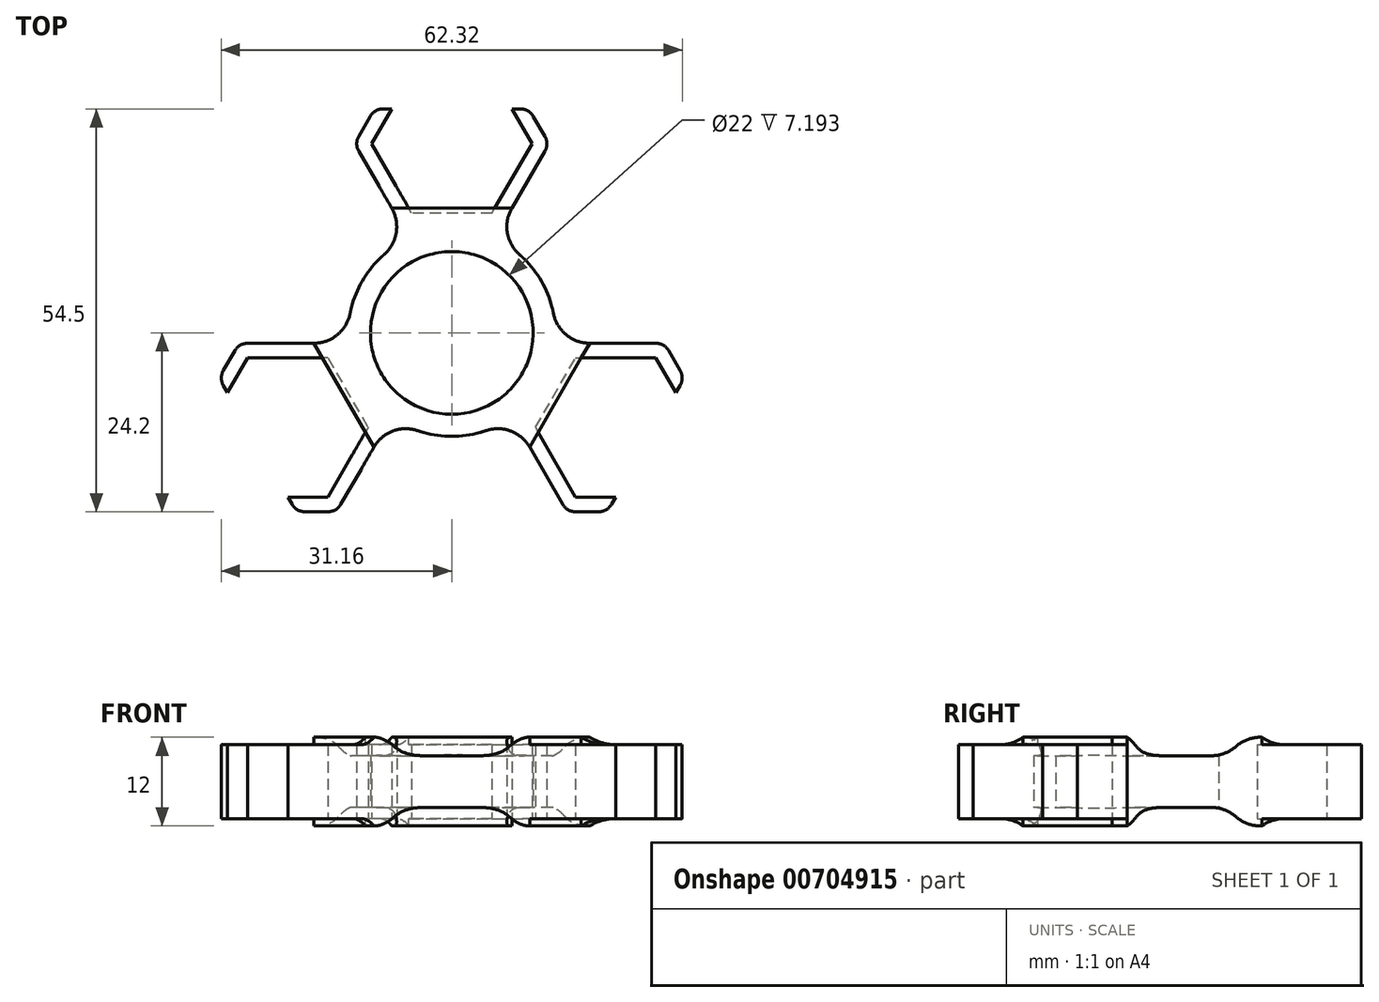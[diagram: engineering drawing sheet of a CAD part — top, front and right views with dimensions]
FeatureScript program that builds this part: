
annotation { "Feature Type Name" : "Feature", "Feature Type Description" : "" }
export const myFeature = defineFeature(function(context is Context, id is Id, definition is map)
    precondition{}
    {
        {
            var Q0;
            Q0=qCreatedBy(makeId("Top.planeOp"),FACE);
            var sketch = newSketch(context, id + "F0", { "sketchPlane" : qUnion([Q0])});
            skArc(sketch, "E0", {"start": v(9.53, 5.5) * mm, "mid": v(0, 11) * mm, "end": v(-9.53, 5.5) * mm});
            skCircle(sketch, "E1.cCircle", {"center": v(0, 25.6) * mm, "radius": 9.4 * mm, "construction": true});
            skLineSegment(sketch, "E1.0", {"start": v(-5.43, 35) * mm, "end": v(5.43, 35) * mm, "construction": true});
            skLineSegment(sketch, "E1.1", {"start": v(5.43, 35) * mm, "end": v(10.85, 25.6) * mm, "construction": true});
            skLineSegment(sketch, "E1.2", {"start": v(10.85, 25.6) * mm, "end": v(5.43, 16.2) * mm});
            skLineSegment(sketch, "E1.3", {"start": v(5.43, 16.2) * mm, "end": v(-5.43, 16.2) * mm});
            skLineSegment(sketch, "E1.4", {"start": v(-5.43, 16.2) * mm, "end": v(-10.85, 25.6) * mm});
            skLineSegment(sketch, "E1.5", {"start": v(-10.85, 25.6) * mm, "end": v(-5.43, 35) * mm, "construction": true});
            skPoint(sketch, "E1.0.midPoint", {"position": v(0, 35) * mm});
            skLineSegment(sketch, "E2", {"start": v(0, 0) * mm, "end": v(-9.53, 5.5) * mm, "construction": true});
            skLineSegment(sketch, "E3", {"start": v(9.53, 5.5) * mm, "end": v(0, 0) * mm, "construction": true});
            skLineSegment(sketch, "E4", {"start": v(-8.14, 30.3) * mm, "end": v(-9.3, 30.3) * mm});
            skArc(sketch, "E5", {"start": v(12.12, 7) * mm, "mid": v(9.4, 10.38) * mm, "end": v(5.75, 12.76) * mm});
            skLineSegment(sketch, "E6.0", {"start": v(-12.59, 26.6) * mm, "end": v(-11.03, 29.3) * mm});
            skLineSegment(sketch, "E6.1", {"start": v(-5.75, 12.76) * mm, "end": v(-12.59, 24.6) * mm});
            skPoint(sketch, "E7.visualSharp", {"position": v(-13.16, 25.6) * mm});
            skArc(sketch, "E7.filletArc", {"start": v(-12.59, 26.6) * mm, "mid": v(-12.85, 25.6) * mm, "end": v(-12.59, 24.6) * mm});
            skPoint(sketch, "E8.visualSharp", {"position": v(-10.45, 30.3) * mm});
            skArc(sketch, "E8.filletArc", {"start": v(-9.3, 30.3) * mm, "mid": v(-10.3, 30.03) * mm, "end": v(-11.03, 29.3) * mm});
            skLineSegment(sketch, "E9", {"start": v(0, 0) * mm, "end": v(0, 25.6) * mm, "construction": true});
            skLineSegment(sketch, "E10.MirrorCS", {"start": v(8.14, 30.3) * mm, "end": v(9.3, 30.3) * mm});
            skArc(sketch, "E11.MirrorCS", {"start": v(9.3, 30.3) * mm, "mid": v(10.3, 30.03) * mm, "end": v(11.03, 29.3) * mm});
            skLineSegment(sketch, "E12.MirrorCS", {"start": v(12.59, 26.6) * mm, "end": v(11.03, 29.3) * mm});
            skArc(sketch, "E13.MirrorCS", {"start": v(12.59, 26.6) * mm, "mid": v(12.85, 25.6) * mm, "end": v(12.59, 24.6) * mm});
            skLineSegment(sketch, "E14.MirrorCS", {"start": v(5.75, 12.76) * mm, "end": v(12.59, 24.6) * mm});
            skArc(sketch, "E15.trimOffspring", {"start": v(-5.75, 12.76) * mm, "mid": v(-9.4, 10.38) * mm, "end": v(-12.12, 7) * mm});
            skLineSegment(sketch, "E16", {"start": v(-8.14, 30.3) * mm, "end": v(-10.85, 25.6) * mm});
            skLineSegment(sketch, "E17", {"start": v(8.14, 30.3) * mm, "end": v(10.85, 25.6) * mm});
            skArc(sketch, "E18.1.0", {"start": v(-9.53, 5.5) * mm, "mid": v(-9.53, -5.5) * mm, "end": v(0, -11) * mm});
            skArc(sketch, "E18.1.1", {"start": v(-8.18, -11.36) * mm, "mid": v(-4.3, -13.32) * mm, "end": v(0, -14) * mm});
            skLineSegment(sketch, "E18.1.2", {"start": v(-8.18, -11.36) * mm, "end": v(-15.01, -23.2) * mm});
            skArc(sketch, "E18.1.3", {"start": v(-12.12, 7) * mm, "mid": v(-13.69, 2.94) * mm, "end": v(-13.93, -1.4) * mm});
            skLineSegment(sketch, "E18.1.4", {"start": v(-13.93, -1.4) * mm, "end": v(-27.6, -1.4) * mm});
            skLineSegment(sketch, "E18.1.5", {"start": v(-27.6, -3.4) * mm, "end": v(-16.74, -3.4) * mm});
            skLineSegment(sketch, "E18.1.6", {"start": v(-16.74, -3.4) * mm, "end": v(-11.32, -12.8) * mm});
            skLineSegment(sketch, "E18.1.7", {"start": v(-11.32, -12.8) * mm, "end": v(-16.74, -22.2) * mm});
            skArc(sketch, "E18.1.8", {"start": v(-16.74, -24.2) * mm, "mid": v(-15.74, -23.93) * mm, "end": v(-15.01, -23.2) * mm});
            skLineSegment(sketch, "E18.1.9", {"start": v(-16.74, -24.2) * mm, "end": v(-19.86, -24.2) * mm});
            skArc(sketch, "E18.1.10", {"start": v(-21.6, -23.2) * mm, "mid": v(-20.86, -23.93) * mm, "end": v(-19.86, -24.2) * mm});
            skLineSegment(sketch, "E18.1.11", {"start": v(-22.17, -22.2) * mm, "end": v(-21.6, -23.2) * mm});
            skLineSegment(sketch, "E18.1.12", {"start": v(-30.31, -8.1) * mm, "end": v(-30.89, -7.1) * mm});
            skArc(sketch, "E18.1.13", {"start": v(-30.89, -7.1) * mm, "mid": v(-31.16, -6.1) * mm, "end": v(-30.89, -5.1) * mm});
            skLineSegment(sketch, "E18.1.14", {"start": v(-29.33, -2.4) * mm, "end": v(-30.89, -5.1) * mm});
            skArc(sketch, "E18.1.15", {"start": v(-29.33, -2.4) * mm, "mid": v(-28.6, -1.67) * mm, "end": v(-27.6, -1.4) * mm});
            skArc(sketch, "E18.2.0", {"start": v(0, -11) * mm, "mid": v(9.53, -5.5) * mm, "end": v(9.53, 5.5) * mm});
            skArc(sketch, "E18.2.1", {"start": v(13.93, -1.4) * mm, "mid": v(13.69, 2.94) * mm, "end": v(12.12, 7) * mm});
            skLineSegment(sketch, "E18.2.2", {"start": v(13.93, -1.4) * mm, "end": v(27.6, -1.4) * mm});
            skArc(sketch, "E18.2.3", {"start": v(0, -14) * mm, "mid": v(4.3, -13.32) * mm, "end": v(8.18, -11.36) * mm});
            skLineSegment(sketch, "E18.2.4", {"start": v(8.18, -11.36) * mm, "end": v(15.01, -23.2) * mm});
            skLineSegment(sketch, "E18.2.5", {"start": v(16.74, -22.2) * mm, "end": v(11.32, -12.8) * mm});
            skLineSegment(sketch, "E18.2.6", {"start": v(11.32, -12.8) * mm, "end": v(16.74, -3.4) * mm});
            skLineSegment(sketch, "E18.2.7", {"start": v(16.74, -3.4) * mm, "end": v(27.6, -3.4) * mm});
            skArc(sketch, "E18.2.8", {"start": v(29.33, -2.4) * mm, "mid": v(28.6, -1.67) * mm, "end": v(27.6, -1.4) * mm});
            skLineSegment(sketch, "E18.2.9", {"start": v(29.33, -2.4) * mm, "end": v(30.89, -5.1) * mm});
            skArc(sketch, "E18.2.10", {"start": v(30.89, -7.1) * mm, "mid": v(31.16, -6.1) * mm, "end": v(30.89, -5.1) * mm});
            skLineSegment(sketch, "E18.2.11", {"start": v(30.31, -8.1) * mm, "end": v(30.89, -7.1) * mm});
            skLineSegment(sketch, "E18.2.12", {"start": v(22.17, -22.2) * mm, "end": v(21.6, -23.2) * mm});
            skArc(sketch, "E18.2.13", {"start": v(21.6, -23.2) * mm, "mid": v(20.86, -23.93) * mm, "end": v(19.86, -24.2) * mm});
            skLineSegment(sketch, "E18.2.14", {"start": v(16.74, -24.2) * mm, "end": v(19.86, -24.2) * mm});
            skArc(sketch, "E18.2.15", {"start": v(16.74, -24.2) * mm, "mid": v(15.74, -23.93) * mm, "end": v(15.01, -23.2) * mm});
            skLineSegment(sketch, "E19", {"start": v(27.6, -3.4) * mm, "end": v(30.31, -8.1) * mm});
            skLineSegment(sketch, "E20", {"start": v(16.74, -22.2) * mm, "end": v(22.17, -22.2) * mm});
            skLineSegment(sketch, "E21", {"start": v(-16.74, -22.2) * mm, "end": v(-22.17, -22.2) * mm});
            skLineSegment(sketch, "E22", {"start": v(-27.6, -3.4) * mm, "end": v(-30.31, -8.1) * mm});
            skSolve(sketch);
        }
        {
            var Q0;
            Q0 = qSketchRegion(id + "F0", true);
            extrude(context, id + "F1", {"entities" : qUnion([Q0]), "endBound" : BoundingType.SYMMETRIC, "depth" : 7 * mm, "offsetDistance" : 25 * mm});
        }
        {
            var Q0;
            Q0=makeQuery(id+"F1.opExtrude","SWEPT_EDGE",EDGE,{"disambiguationData":[OSD([sQuery(id+"F0.wireOp",EDGE,"E18.1.1"),sQuery(id+"F0.wireOp",EDGE,"E18.1.2")])]});
            var Q1;
            Q1=makeQuery(id+"F1.opExtrude","SWEPT_EDGE",EDGE,{"disambiguationData":[OSD([sQuery(id+"F0.wireOp",EDGE,"E18.2.3"),sQuery(id+"F0.wireOp",EDGE,"E18.2.4")])]});
            var Q2;
            Q2=makeQuery(id+"F1.opExtrude","SWEPT_EDGE",EDGE,{"disambiguationData":[OSD([sQuery(id+"F0.wireOp",EDGE,"E18.2.1"),sQuery(id+"F0.wireOp",EDGE,"E18.2.2")])]});
            var Q3;
            Q3=makeQuery(id+"F1.opExtrude","SWEPT_EDGE",EDGE,{"disambiguationData":[OSD([sQuery(id+"F0.wireOp",EDGE,"E5"),sQuery(id+"F0.wireOp",EDGE,"E14.MirrorCS")])]});
            var Q4;
            Q4=makeQuery(id+"F1.opExtrude","SWEPT_EDGE",EDGE,{"disambiguationData":[OSD([sQuery(id+"F0.wireOp",EDGE,"E6.1"),sQuery(id+"F0.wireOp",EDGE,"E15.trimOffspring")])]});
            var Q5;
            Q5=makeQuery(id+"F1.opExtrude","SWEPT_EDGE",EDGE,{"disambiguationData":[OSD([sQuery(id+"F0.wireOp",EDGE,"E18.1.3"),sQuery(id+"F0.wireOp",EDGE,"E18.1.4")])]});
            fillet(context, id + "F2", {"entities" : qUnion([Q0, Q1, Q2, Q3, Q4, Q5]), "radius" : 5 * mm, "tangentPropagation" : true, "allowEdgeOverflow" : false});
        }
        {
            var Q0;
            Q0=qCreatedBy(makeId("Top.planeOp"),FACE);
            var sketch = newSketch(context, id + "F3", { "sketchPlane" : qUnion([Q0])});
            skLineSegment(sketch, "E23.0", {"start": v(-12.59, 26.6) * mm, "end": v(-11.03, 29.3) * mm});
            skArc(sketch, "E23.1", {"start": v(-12.59, 26.6) * mm, "mid": v(-12.85, 25.6) * mm, "end": v(-12.59, 24.6) * mm});
            skLineSegment(sketch, "E23.2", {"start": v(-8.12, 16.86) * mm, "end": v(-12.59, 24.6) * mm});
            skLineSegment(sketch, "E23.3", {"start": v(-5.43, 16.2) * mm, "end": v(-10.85, 25.6) * mm});
            skLineSegment(sketch, "E23.4", {"start": v(-8.14, 30.3) * mm, "end": v(-10.85, 25.6) * mm});
            skArc(sketch, "E23.5", {"start": v(-9.3, 30.3) * mm, "mid": v(-10.3, 30.03) * mm, "end": v(-11.03, 29.3) * mm});
            skLineSegment(sketch, "E23.6", {"start": v(-8.14, 30.3) * mm, "end": v(-9.3, 30.3) * mm});
            skLineSegment(sketch, "E24", {"start": v(0, 15.22) * mm, "end": v(0, 32.5) * mm, "construction": true});
            skLineSegment(sketch, "E25.MirrorCS", {"start": v(5.43, 16.2) * mm, "end": v(10.85, 25.6) * mm});
            skLineSegment(sketch, "E26.MirrorCS", {"start": v(8.12, 16.86) * mm, "end": v(12.59, 24.6) * mm});
            skArc(sketch, "E27.MirrorCS", {"start": v(12.59, 26.6) * mm, "mid": v(12.85, 25.6) * mm, "end": v(12.59, 24.6) * mm});
            skLineSegment(sketch, "E28.MirrorCS", {"start": v(8.14, 30.3) * mm, "end": v(10.85, 25.6) * mm});
            skLineSegment(sketch, "E29.MirrorCS", {"start": v(12.59, 26.6) * mm, "end": v(11.03, 29.3) * mm});
            skArc(sketch, "E30.MirrorCS", {"start": v(9.3, 30.3) * mm, "mid": v(10.3, 30.03) * mm, "end": v(11.03, 29.3) * mm});
            skLineSegment(sketch, "E31.MirrorCS", {"start": v(8.14, 30.3) * mm, "end": v(9.3, 30.3) * mm});
            skLineSegment(sketch, "E32", {"start": v(5.43, 16.2) * mm, "end": v(-5.43, 16.2) * mm});
            skArc(sketch, "E33.0", {"start": v(8.12, 16.86) * mm, "mid": v(7.62, 15.65) * mm, "end": v(7.45, 14.36) * mm});
            skArc(sketch, "E33.1", {"start": v(-7.45, 14.36) * mm, "mid": v(-7.62, 15.65) * mm, "end": v(-8.12, 16.86) * mm});
            skLineSegment(sketch, "E34", {"start": v(7.45, 14.36) * mm, "end": v(-7.45, 14.36) * mm});
            skPoint(sketch, "E35.orphan", {"position": v(9.17, 10.58) * mm});
            skPoint(sketch, "E36.orphan", {"position": v(-9.17, 10.58) * mm});
            skLineSegment(sketch, "E37.1.0", {"start": v(13.18, -7.6) * mm, "end": v(28.15, -16.25) * mm, "construction": true});
            skLineSegment(sketch, "E37.1.1", {"start": v(18.66, -1.4) * mm, "end": v(27.6, -1.4) * mm});
            skLineSegment(sketch, "E37.1.2", {"start": v(11.32, -12.8) * mm, "end": v(16.74, -3.4) * mm});
            skLineSegment(sketch, "E37.1.3", {"start": v(8.71, -13.63) * mm, "end": v(16.16, -0.73) * mm});
            skLineSegment(sketch, "E37.1.4", {"start": v(10.54, -15.46) * mm, "end": v(15.01, -23.2) * mm});
            skLineSegment(sketch, "E37.1.5", {"start": v(11.32, -12.8) * mm, "end": v(16.74, -22.2) * mm});
            skLineSegment(sketch, "E37.1.6", {"start": v(16.74, -3.4) * mm, "end": v(27.6, -3.4) * mm});
            skLineSegment(sketch, "E37.1.7", {"start": v(30.31, -8.1) * mm, "end": v(27.6, -3.4) * mm});
            skLineSegment(sketch, "E37.1.8", {"start": v(22.17, -22.2) * mm, "end": v(16.74, -22.2) * mm});
            skLineSegment(sketch, "E37.1.9", {"start": v(29.33, -2.4) * mm, "end": v(30.89, -5.1) * mm});
            skLineSegment(sketch, "E37.1.10", {"start": v(30.31, -8.1) * mm, "end": v(30.89, -7.1) * mm});
            skArc(sketch, "E37.1.11", {"start": v(16.16, -0.73) * mm, "mid": v(17.36, -1.23) * mm, "end": v(18.66, -1.4) * mm});
            skArc(sketch, "E37.1.12", {"start": v(29.33, -2.4) * mm, "mid": v(28.6, -1.67) * mm, "end": v(27.6, -1.4) * mm});
            skLineSegment(sketch, "E37.1.13", {"start": v(22.17, -22.2) * mm, "end": v(21.6, -23.2) * mm});
            skArc(sketch, "E37.1.14", {"start": v(21.6, -23.2) * mm, "mid": v(20.86, -23.93) * mm, "end": v(19.86, -24.2) * mm});
            skArc(sketch, "E37.1.15", {"start": v(30.89, -7.1) * mm, "mid": v(31.16, -6.1) * mm, "end": v(30.89, -5.1) * mm});
            skArc(sketch, "E37.1.16", {"start": v(10.54, -15.46) * mm, "mid": v(9.75, -14.42) * mm, "end": v(8.71, -13.63) * mm});
            skLineSegment(sketch, "E37.1.17", {"start": v(16.74, -24.2) * mm, "end": v(19.86, -24.2) * mm});
            skArc(sketch, "E37.1.18", {"start": v(16.74, -24.2) * mm, "mid": v(15.74, -23.93) * mm, "end": v(15.01, -23.2) * mm});
            skLineSegment(sketch, "E37.2.0", {"start": v(-13.18, -7.6) * mm, "end": v(-28.15, -16.25) * mm, "construction": true});
            skLineSegment(sketch, "E37.2.1", {"start": v(-10.54, -15.46) * mm, "end": v(-15.01, -23.2) * mm});
            skLineSegment(sketch, "E37.2.2", {"start": v(-16.74, -3.4) * mm, "end": v(-11.32, -12.8) * mm});
            skLineSegment(sketch, "E37.2.3", {"start": v(-16.16, -0.73) * mm, "end": v(-8.71, -13.63) * mm});
            skLineSegment(sketch, "E37.2.4", {"start": v(-18.66, -1.4) * mm, "end": v(-27.6, -1.4) * mm});
            skLineSegment(sketch, "E37.2.5", {"start": v(-16.74, -3.4) * mm, "end": v(-27.6, -3.4) * mm});
            skLineSegment(sketch, "E37.2.6", {"start": v(-11.32, -12.8) * mm, "end": v(-16.74, -22.2) * mm});
            skLineSegment(sketch, "E37.2.7", {"start": v(-22.17, -22.2) * mm, "end": v(-16.74, -22.2) * mm});
            skLineSegment(sketch, "E37.2.8", {"start": v(-30.31, -8.1) * mm, "end": v(-27.6, -3.4) * mm});
            skLineSegment(sketch, "E37.2.9", {"start": v(-16.74, -24.2) * mm, "end": v(-19.86, -24.2) * mm});
            skLineSegment(sketch, "E37.2.10", {"start": v(-22.17, -22.2) * mm, "end": v(-21.6, -23.2) * mm});
            skArc(sketch, "E37.2.11", {"start": v(-8.71, -13.63) * mm, "mid": v(-9.75, -14.42) * mm, "end": v(-10.54, -15.46) * mm});
            skArc(sketch, "E37.2.12", {"start": v(-16.74, -24.2) * mm, "mid": v(-15.74, -23.93) * mm, "end": v(-15.01, -23.2) * mm});
            skLineSegment(sketch, "E37.2.13", {"start": v(-30.31, -8.1) * mm, "end": v(-30.89, -7.1) * mm});
            skArc(sketch, "E37.2.14", {"start": v(-30.89, -7.1) * mm, "mid": v(-31.16, -6.1) * mm, "end": v(-30.89, -5.1) * mm});
            skArc(sketch, "E37.2.15", {"start": v(-21.6, -23.2) * mm, "mid": v(-20.86, -23.93) * mm, "end": v(-19.86, -24.2) * mm});
            skArc(sketch, "E37.2.16", {"start": v(-18.66, -1.4) * mm, "mid": v(-17.36, -1.23) * mm, "end": v(-16.16, -0.73) * mm});
            skLineSegment(sketch, "E37.2.17", {"start": v(-29.33, -2.4) * mm, "end": v(-30.89, -5.1) * mm});
            skArc(sketch, "E37.2.18", {"start": v(-29.33, -2.4) * mm, "mid": v(-28.6, -1.67) * mm, "end": v(-27.6, -1.4) * mm});
            skPoint(sketch, "E37.center", {"position": v(0, 0) * mm});
            skLineSegment(sketch, "E37.anchor1", {"start": v(0, 0) * mm, "end": v(0, 32.5) * mm, "construction": true});
            skLineSegment(sketch, "E37.anchor2", {"start": v(0, 0) * mm, "end": v(-28.15, -16.25) * mm, "construction": true});
            skSolve(sketch);
        }
        {
            var Q0;
            Q0 = qSketchRegion(id + "F3", true);
            extrude(context, id + "F4", {"entities" : qUnion([Q0]), "operationType" : NewBodyOperationType.ADD, "endBound" : BoundingType.SYMMETRIC, "depth" : 10 * mm, "offsetDistance" : 25 * mm});
        }
        {
            var Q0;
            Q0=makeQuery(id+"F4.opExtrude","CAP_FACE",FACE,{"disambiguationData":[OSD([sQuery(id+"F3.wireOp",EDGE,"E23.0"),sQuery(id+"F3.wireOp",EDGE,"E23.1"),sQuery(id+"F3.wireOp",EDGE,"E23.2"),sQuery(id+"F3.wireOp",EDGE,"E23.3"),sQuery(id+"F3.wireOp",EDGE,"E23.4"),sQuery(id+"F3.wireOp",EDGE,"E23.5"),sQuery(id+"F3.wireOp",EDGE,"E23.6"),sQuery(id+"F3.wireOp",EDGE,"E25.MirrorCS"),sQuery(id+"F3.wireOp",EDGE,"E26.MirrorCS"),sQuery(id+"F3.wireOp",EDGE,"E27.MirrorCS"),sQuery(id+"F3.wireOp",EDGE,"E28.MirrorCS"),sQuery(id+"F3.wireOp",EDGE,"E29.MirrorCS"),sQuery(id+"F3.wireOp",EDGE,"E30.MirrorCS"),sQuery(id+"F3.wireOp",EDGE,"E31.MirrorCS"),sQuery(id+"F3.wireOp",EDGE,"E32"),sQuery(id+"F3.wireOp",EDGE,"E33.0"),sQuery(id+"F3.wireOp",EDGE,"E33.1"),sQuery(id+"F3.wireOp",EDGE,"E34")])],"isStart":false});
            var sketch = newSketch(context, id + "F5", { "sketchPlane" : qUnion([Q0])});
            skLineSegment(sketch, "E38.2", {"start": v(7.45, 14.36) * mm, "end": v(-7.45, 14.36) * mm});
            skArc(sketch, "E38.3", {"start": v(8.12, 16.86) * mm, "mid": v(7.62, 15.65) * mm, "end": v(7.45, 14.36) * mm});
            skArc(sketch, "E38.4", {"start": v(-7.45, 14.36) * mm, "mid": v(-7.62, 15.65) * mm, "end": v(-8.12, 16.86) * mm});
            skLineSegment(sketch, "E39", {"start": v(-8.12, 16.86) * mm, "end": v(8.12, 16.86) * mm});
            skPoint(sketch, "E38.6.end.orphan", {"position": v(-12.59, 24.6) * mm});
            skPoint(sketch, "E40.orphan", {"position": v(-10.85, 25.6) * mm});
            skPoint(sketch, "E41.orphan", {"position": v(10.85, 25.6) * mm});
            skPoint(sketch, "E38.7.end.orphan", {"position": v(12.59, 24.6) * mm});
            skPoint(sketch, "E38.1.end.orphan", {"position": v(-5.43, 16.2) * mm});
            skPoint(sketch, "E38.5.start.orphan", {"position": v(5.43, 16.2) * mm});
            skPoint(sketch, "E42.1.0", {"position": v(-11.32, -12.8) * mm});
            skLineSegment(sketch, "E42.1.1", {"start": v(-10.54, -15.46) * mm, "end": v(-18.66, -1.4) * mm});
            skPoint(sketch, "E42.1.2", {"position": v(-16.74, -3.4) * mm});
            skArc(sketch, "E42.1.3", {"start": v(-8.71, -13.63) * mm, "mid": v(-9.75, -14.42) * mm, "end": v(-10.54, -15.46) * mm});
            skArc(sketch, "E42.1.4", {"start": v(-18.66, -1.4) * mm, "mid": v(-17.36, -1.23) * mm, "end": v(-16.16, -0.73) * mm});
            skLineSegment(sketch, "E42.1.5", {"start": v(-16.16, -0.73) * mm, "end": v(-8.71, -13.63) * mm});
            skPoint(sketch, "E42.2.0", {"position": v(16.74, -3.4) * mm});
            skLineSegment(sketch, "E42.2.1", {"start": v(18.66, -1.4) * mm, "end": v(10.54, -15.46) * mm});
            skPoint(sketch, "E42.2.2", {"position": v(11.32, -12.8) * mm});
            skArc(sketch, "E42.2.3", {"start": v(16.16, -0.73) * mm, "mid": v(17.36, -1.23) * mm, "end": v(18.66, -1.4) * mm});
            skArc(sketch, "E42.2.4", {"start": v(10.54, -15.46) * mm, "mid": v(9.75, -14.42) * mm, "end": v(8.71, -13.63) * mm});
            skLineSegment(sketch, "E42.2.5", {"start": v(8.71, -13.63) * mm, "end": v(16.16, -0.73) * mm});
            skPoint(sketch, "E42.center", {"position": v(0, 0) * mm});
            skSolve(sketch);
        }
        {
            var Q0;
            Q0 = qSketchRegion(id + "F5", true);
            extrude(context, id + "F6", {"entities" : qUnion([Q0]), "depth" : 1 * mm, "offsetDistance" : 25 * mm});
        }
        {
            var Q0;
            Q0=makeQuery(id+"F6.opExtrude","SWEPT_BODY",BODY,{"disambiguationData":[OSD([sQuery(id+"F5.wireOp",EDGE,"E38.2"),sQuery(id+"F5.wireOp",EDGE,"E38.3"),sQuery(id+"F5.wireOp",EDGE,"E38.4"),sQuery(id+"F5.wireOp",EDGE,"E39")])]});
            var Q1;
            Q1=makeQuery(id+"F6.opExtrude","SWEPT_BODY",BODY,{"disambiguationData":[OSD([sQuery(id+"F5.wireOp",EDGE,"E42.1.1"),sQuery(id+"F5.wireOp",EDGE,"E42.1.3"),sQuery(id+"F5.wireOp",EDGE,"E42.1.4"),sQuery(id+"F5.wireOp",EDGE,"E42.1.5")])]});
            var Q2;
            Q2=makeQuery(id+"F6.opExtrude","SWEPT_BODY",BODY,{"disambiguationData":[OSD([sQuery(id+"F5.wireOp",EDGE,"E42.2.1"),sQuery(id+"F5.wireOp",EDGE,"E42.2.3"),sQuery(id+"F5.wireOp",EDGE,"E42.2.4"),sQuery(id+"F5.wireOp",EDGE,"E42.2.5")])]});
            var Q3;
            Q3=qCreatedBy(makeId("Top.planeOp"),FACE);
            mirror(context, id + "F7", {"operationType" : NewBodyOperationType.ADD, "entities" : qUnion([Q0, Q1, Q2]), "mirrorPlane" : qUnion([Q3])});
        }
        {
            var Q0;
            Q0=makeQuery(id+"F4.boolean.opBoolean","INTERSECT",EDGE,{"derivedFrom":[makeQuery(id+"F1.opExtrude","CAP_FACE",FACE,{"disambiguationData":[OSD([sQuery(id+"F0.wireOp",EDGE,"E0"),sQuery(id+"F0.wireOp",EDGE,"E1.2"),sQuery(id+"F0.wireOp",EDGE,"E1.3"),sQuery(id+"F0.wireOp",EDGE,"E1.4"),sQuery(id+"F0.wireOp",EDGE,"E4"),sQuery(id+"F0.wireOp",EDGE,"E5"),sQuery(id+"F0.wireOp",EDGE,"E6.0"),sQuery(id+"F0.wireOp",EDGE,"E6.1"),sQuery(id+"F0.wireOp",EDGE,"E7.filletArc"),sQuery(id+"F0.wireOp",EDGE,"E8.filletArc"),sQuery(id+"F0.wireOp",EDGE,"E10.MirrorCS"),sQuery(id+"F0.wireOp",EDGE,"E11.MirrorCS"),sQuery(id+"F0.wireOp",EDGE,"E12.MirrorCS"),sQuery(id+"F0.wireOp",EDGE,"E13.MirrorCS"),sQuery(id+"F0.wireOp",EDGE,"E14.MirrorCS"),sQuery(id+"F0.wireOp",EDGE,"E15.trimOffspring"),sQuery(id+"F0.wireOp",EDGE,"E16"),sQuery(id+"F0.wireOp",EDGE,"E17"),sQuery(id+"F0.wireOp",EDGE,"E18.1.0"),sQuery(id+"F0.wireOp",EDGE,"E18.1.1"),sQuery(id+"F0.wireOp",EDGE,"E18.1.2"),sQuery(id+"F0.wireOp",EDGE,"E18.1.3"),sQuery(id+"F0.wireOp",EDGE,"E18.1.4"),sQuery(id+"F0.wireOp",EDGE,"E18.1.5"),sQuery(id+"F0.wireOp",EDGE,"E18.1.6"),sQuery(id+"F0.wireOp",EDGE,"E18.1.7"),sQuery(id+"F0.wireOp",EDGE,"E18.1.8"),sQuery(id+"F0.wireOp",EDGE,"E18.1.9"),sQuery(id+"F0.wireOp",EDGE,"E18.1.10"),sQuery(id+"F0.wireOp",EDGE,"E18.1.11"),sQuery(id+"F0.wireOp",EDGE,"E18.1.12"),sQuery(id+"F0.wireOp",EDGE,"E18.1.13"),sQuery(id+"F0.wireOp",EDGE,"E18.1.14"),sQuery(id+"F0.wireOp",EDGE,"E18.1.15"),sQuery(id+"F0.wireOp",EDGE,"E18.2.0"),sQuery(id+"F0.wireOp",EDGE,"E18.2.1"),sQuery(id+"F0.wireOp",EDGE,"E18.2.2"),sQuery(id+"F0.wireOp",EDGE,"E18.2.3"),sQuery(id+"F0.wireOp",EDGE,"E18.2.4"),sQuery(id+"F0.wireOp",EDGE,"E18.2.5"),sQuery(id+"F0.wireOp",EDGE,"E18.2.6"),sQuery(id+"F0.wireOp",EDGE,"E18.2.7"),sQuery(id+"F0.wireOp",EDGE,"E18.2.8"),sQuery(id+"F0.wireOp",EDGE,"E18.2.9"),sQuery(id+"F0.wireOp",EDGE,"E18.2.10"),sQuery(id+"F0.wireOp",EDGE,"E18.2.11"),sQuery(id+"F0.wireOp",EDGE,"E18.2.12"),sQuery(id+"F0.wireOp",EDGE,"E18.2.13"),sQuery(id+"F0.wireOp",EDGE,"E18.2.14"),sQuery(id+"F0.wireOp",EDGE,"E18.2.15"),sQuery(id+"F0.wireOp",EDGE,"E19"),sQuery(id+"F0.wireOp",EDGE,"E20"),sQuery(id+"F0.wireOp",EDGE,"E21"),sQuery(id+"F0.wireOp",EDGE,"E22")])],"isStart":true}),makeQuery(id+"F4.opExtrude","SWEPT_FACE",FACE,{"disambiguationData":[OSD([sQuery(id+"F3.wireOp",EDGE,"E34")])]})]});
            var Q1;
            Q1=makeQuery(id+"F4.boolean.opBoolean","INTERSECT",EDGE,{"derivedFrom":[makeQuery(id+"F1.opExtrude","CAP_FACE",FACE,{"disambiguationData":[OSD([sQuery(id+"F0.wireOp",EDGE,"E0"),sQuery(id+"F0.wireOp",EDGE,"E1.2"),sQuery(id+"F0.wireOp",EDGE,"E1.3"),sQuery(id+"F0.wireOp",EDGE,"E1.4"),sQuery(id+"F0.wireOp",EDGE,"E4"),sQuery(id+"F0.wireOp",EDGE,"E5"),sQuery(id+"F0.wireOp",EDGE,"E6.0"),sQuery(id+"F0.wireOp",EDGE,"E6.1"),sQuery(id+"F0.wireOp",EDGE,"E7.filletArc"),sQuery(id+"F0.wireOp",EDGE,"E8.filletArc"),sQuery(id+"F0.wireOp",EDGE,"E10.MirrorCS"),sQuery(id+"F0.wireOp",EDGE,"E11.MirrorCS"),sQuery(id+"F0.wireOp",EDGE,"E12.MirrorCS"),sQuery(id+"F0.wireOp",EDGE,"E13.MirrorCS"),sQuery(id+"F0.wireOp",EDGE,"E14.MirrorCS"),sQuery(id+"F0.wireOp",EDGE,"E15.trimOffspring"),sQuery(id+"F0.wireOp",EDGE,"E16"),sQuery(id+"F0.wireOp",EDGE,"E17"),sQuery(id+"F0.wireOp",EDGE,"E18.1.0"),sQuery(id+"F0.wireOp",EDGE,"E18.1.1"),sQuery(id+"F0.wireOp",EDGE,"E18.1.2"),sQuery(id+"F0.wireOp",EDGE,"E18.1.3"),sQuery(id+"F0.wireOp",EDGE,"E18.1.4"),sQuery(id+"F0.wireOp",EDGE,"E18.1.5"),sQuery(id+"F0.wireOp",EDGE,"E18.1.6"),sQuery(id+"F0.wireOp",EDGE,"E18.1.7"),sQuery(id+"F0.wireOp",EDGE,"E18.1.8"),sQuery(id+"F0.wireOp",EDGE,"E18.1.9"),sQuery(id+"F0.wireOp",EDGE,"E18.1.10"),sQuery(id+"F0.wireOp",EDGE,"E18.1.11"),sQuery(id+"F0.wireOp",EDGE,"E18.1.12"),sQuery(id+"F0.wireOp",EDGE,"E18.1.13"),sQuery(id+"F0.wireOp",EDGE,"E18.1.14"),sQuery(id+"F0.wireOp",EDGE,"E18.1.15"),sQuery(id+"F0.wireOp",EDGE,"E18.2.0"),sQuery(id+"F0.wireOp",EDGE,"E18.2.1"),sQuery(id+"F0.wireOp",EDGE,"E18.2.2"),sQuery(id+"F0.wireOp",EDGE,"E18.2.3"),sQuery(id+"F0.wireOp",EDGE,"E18.2.4"),sQuery(id+"F0.wireOp",EDGE,"E18.2.5"),sQuery(id+"F0.wireOp",EDGE,"E18.2.6"),sQuery(id+"F0.wireOp",EDGE,"E18.2.7"),sQuery(id+"F0.wireOp",EDGE,"E18.2.8"),sQuery(id+"F0.wireOp",EDGE,"E18.2.9"),sQuery(id+"F0.wireOp",EDGE,"E18.2.10"),sQuery(id+"F0.wireOp",EDGE,"E18.2.11"),sQuery(id+"F0.wireOp",EDGE,"E18.2.12"),sQuery(id+"F0.wireOp",EDGE,"E18.2.13"),sQuery(id+"F0.wireOp",EDGE,"E18.2.14"),sQuery(id+"F0.wireOp",EDGE,"E18.2.15"),sQuery(id+"F0.wireOp",EDGE,"E19"),sQuery(id+"F0.wireOp",EDGE,"E20"),sQuery(id+"F0.wireOp",EDGE,"E21"),sQuery(id+"F0.wireOp",EDGE,"E22")])],"isStart":true}),makeQuery(id+"F4.opExtrude","SWEPT_FACE",FACE,{"disambiguationData":[OSD([sQuery(id+"F3.wireOp",EDGE,"E37.1.3")])]})]});
            var Q2;
            Q2=makeQuery(id+"F4.boolean.opBoolean","INTERSECT",EDGE,{"derivedFrom":[makeQuery(id+"F1.opExtrude","CAP_FACE",FACE,{"disambiguationData":[OSD([sQuery(id+"F0.wireOp",EDGE,"E0"),sQuery(id+"F0.wireOp",EDGE,"E1.2"),sQuery(id+"F0.wireOp",EDGE,"E1.3"),sQuery(id+"F0.wireOp",EDGE,"E1.4"),sQuery(id+"F0.wireOp",EDGE,"E4"),sQuery(id+"F0.wireOp",EDGE,"E5"),sQuery(id+"F0.wireOp",EDGE,"E6.0"),sQuery(id+"F0.wireOp",EDGE,"E6.1"),sQuery(id+"F0.wireOp",EDGE,"E7.filletArc"),sQuery(id+"F0.wireOp",EDGE,"E8.filletArc"),sQuery(id+"F0.wireOp",EDGE,"E10.MirrorCS"),sQuery(id+"F0.wireOp",EDGE,"E11.MirrorCS"),sQuery(id+"F0.wireOp",EDGE,"E12.MirrorCS"),sQuery(id+"F0.wireOp",EDGE,"E13.MirrorCS"),sQuery(id+"F0.wireOp",EDGE,"E14.MirrorCS"),sQuery(id+"F0.wireOp",EDGE,"E15.trimOffspring"),sQuery(id+"F0.wireOp",EDGE,"E16"),sQuery(id+"F0.wireOp",EDGE,"E17"),sQuery(id+"F0.wireOp",EDGE,"E18.1.0"),sQuery(id+"F0.wireOp",EDGE,"E18.1.1"),sQuery(id+"F0.wireOp",EDGE,"E18.1.2"),sQuery(id+"F0.wireOp",EDGE,"E18.1.3"),sQuery(id+"F0.wireOp",EDGE,"E18.1.4"),sQuery(id+"F0.wireOp",EDGE,"E18.1.5"),sQuery(id+"F0.wireOp",EDGE,"E18.1.6"),sQuery(id+"F0.wireOp",EDGE,"E18.1.7"),sQuery(id+"F0.wireOp",EDGE,"E18.1.8"),sQuery(id+"F0.wireOp",EDGE,"E18.1.9"),sQuery(id+"F0.wireOp",EDGE,"E18.1.10"),sQuery(id+"F0.wireOp",EDGE,"E18.1.11"),sQuery(id+"F0.wireOp",EDGE,"E18.1.12"),sQuery(id+"F0.wireOp",EDGE,"E18.1.13"),sQuery(id+"F0.wireOp",EDGE,"E18.1.14"),sQuery(id+"F0.wireOp",EDGE,"E18.1.15"),sQuery(id+"F0.wireOp",EDGE,"E18.2.0"),sQuery(id+"F0.wireOp",EDGE,"E18.2.1"),sQuery(id+"F0.wireOp",EDGE,"E18.2.2"),sQuery(id+"F0.wireOp",EDGE,"E18.2.3"),sQuery(id+"F0.wireOp",EDGE,"E18.2.4"),sQuery(id+"F0.wireOp",EDGE,"E18.2.5"),sQuery(id+"F0.wireOp",EDGE,"E18.2.6"),sQuery(id+"F0.wireOp",EDGE,"E18.2.7"),sQuery(id+"F0.wireOp",EDGE,"E18.2.8"),sQuery(id+"F0.wireOp",EDGE,"E18.2.9"),sQuery(id+"F0.wireOp",EDGE,"E18.2.10"),sQuery(id+"F0.wireOp",EDGE,"E18.2.11"),sQuery(id+"F0.wireOp",EDGE,"E18.2.12"),sQuery(id+"F0.wireOp",EDGE,"E18.2.13"),sQuery(id+"F0.wireOp",EDGE,"E18.2.14"),sQuery(id+"F0.wireOp",EDGE,"E18.2.15"),sQuery(id+"F0.wireOp",EDGE,"E19"),sQuery(id+"F0.wireOp",EDGE,"E20"),sQuery(id+"F0.wireOp",EDGE,"E21"),sQuery(id+"F0.wireOp",EDGE,"E22")])],"isStart":true}),makeQuery(id+"F4.opExtrude","SWEPT_FACE",FACE,{"disambiguationData":[OSD([sQuery(id+"F3.wireOp",EDGE,"E37.2.3")])]})]});
            var Q3;
            Q3=makeQuery(id+"F4.boolean.opBoolean","INTERSECT",EDGE,{"derivedFrom":[makeQuery(id+"F1.opExtrude","CAP_FACE",FACE,{"disambiguationData":[OSD([sQuery(id+"F0.wireOp",EDGE,"E0"),sQuery(id+"F0.wireOp",EDGE,"E1.2"),sQuery(id+"F0.wireOp",EDGE,"E1.3"),sQuery(id+"F0.wireOp",EDGE,"E1.4"),sQuery(id+"F0.wireOp",EDGE,"E4"),sQuery(id+"F0.wireOp",EDGE,"E5"),sQuery(id+"F0.wireOp",EDGE,"E6.0"),sQuery(id+"F0.wireOp",EDGE,"E6.1"),sQuery(id+"F0.wireOp",EDGE,"E7.filletArc"),sQuery(id+"F0.wireOp",EDGE,"E8.filletArc"),sQuery(id+"F0.wireOp",EDGE,"E10.MirrorCS"),sQuery(id+"F0.wireOp",EDGE,"E11.MirrorCS"),sQuery(id+"F0.wireOp",EDGE,"E12.MirrorCS"),sQuery(id+"F0.wireOp",EDGE,"E13.MirrorCS"),sQuery(id+"F0.wireOp",EDGE,"E14.MirrorCS"),sQuery(id+"F0.wireOp",EDGE,"E15.trimOffspring"),sQuery(id+"F0.wireOp",EDGE,"E16"),sQuery(id+"F0.wireOp",EDGE,"E17"),sQuery(id+"F0.wireOp",EDGE,"E18.1.0"),sQuery(id+"F0.wireOp",EDGE,"E18.1.1"),sQuery(id+"F0.wireOp",EDGE,"E18.1.2"),sQuery(id+"F0.wireOp",EDGE,"E18.1.3"),sQuery(id+"F0.wireOp",EDGE,"E18.1.4"),sQuery(id+"F0.wireOp",EDGE,"E18.1.5"),sQuery(id+"F0.wireOp",EDGE,"E18.1.6"),sQuery(id+"F0.wireOp",EDGE,"E18.1.7"),sQuery(id+"F0.wireOp",EDGE,"E18.1.8"),sQuery(id+"F0.wireOp",EDGE,"E18.1.9"),sQuery(id+"F0.wireOp",EDGE,"E18.1.10"),sQuery(id+"F0.wireOp",EDGE,"E18.1.11"),sQuery(id+"F0.wireOp",EDGE,"E18.1.12"),sQuery(id+"F0.wireOp",EDGE,"E18.1.13"),sQuery(id+"F0.wireOp",EDGE,"E18.1.14"),sQuery(id+"F0.wireOp",EDGE,"E18.1.15"),sQuery(id+"F0.wireOp",EDGE,"E18.2.0"),sQuery(id+"F0.wireOp",EDGE,"E18.2.1"),sQuery(id+"F0.wireOp",EDGE,"E18.2.2"),sQuery(id+"F0.wireOp",EDGE,"E18.2.3"),sQuery(id+"F0.wireOp",EDGE,"E18.2.4"),sQuery(id+"F0.wireOp",EDGE,"E18.2.5"),sQuery(id+"F0.wireOp",EDGE,"E18.2.6"),sQuery(id+"F0.wireOp",EDGE,"E18.2.7"),sQuery(id+"F0.wireOp",EDGE,"E18.2.8"),sQuery(id+"F0.wireOp",EDGE,"E18.2.9"),sQuery(id+"F0.wireOp",EDGE,"E18.2.10"),sQuery(id+"F0.wireOp",EDGE,"E18.2.11"),sQuery(id+"F0.wireOp",EDGE,"E18.2.12"),sQuery(id+"F0.wireOp",EDGE,"E18.2.13"),sQuery(id+"F0.wireOp",EDGE,"E18.2.14"),sQuery(id+"F0.wireOp",EDGE,"E18.2.15"),sQuery(id+"F0.wireOp",EDGE,"E19"),sQuery(id+"F0.wireOp",EDGE,"E20"),sQuery(id+"F0.wireOp",EDGE,"E21"),sQuery(id+"F0.wireOp",EDGE,"E22")])],"isStart":false}),makeQuery(id+"F4.opExtrude","SWEPT_FACE",FACE,{"disambiguationData":[OSD([sQuery(id+"F3.wireOp",EDGE,"E37.1.3")])]})]});
            var Q4;
            Q4=makeQuery(id+"F4.boolean.opBoolean","INTERSECT",EDGE,{"derivedFrom":[makeQuery(id+"F1.opExtrude","CAP_FACE",FACE,{"disambiguationData":[OSD([sQuery(id+"F0.wireOp",EDGE,"E0"),sQuery(id+"F0.wireOp",EDGE,"E1.2"),sQuery(id+"F0.wireOp",EDGE,"E1.3"),sQuery(id+"F0.wireOp",EDGE,"E1.4"),sQuery(id+"F0.wireOp",EDGE,"E4"),sQuery(id+"F0.wireOp",EDGE,"E5"),sQuery(id+"F0.wireOp",EDGE,"E6.0"),sQuery(id+"F0.wireOp",EDGE,"E6.1"),sQuery(id+"F0.wireOp",EDGE,"E7.filletArc"),sQuery(id+"F0.wireOp",EDGE,"E8.filletArc"),sQuery(id+"F0.wireOp",EDGE,"E10.MirrorCS"),sQuery(id+"F0.wireOp",EDGE,"E11.MirrorCS"),sQuery(id+"F0.wireOp",EDGE,"E12.MirrorCS"),sQuery(id+"F0.wireOp",EDGE,"E13.MirrorCS"),sQuery(id+"F0.wireOp",EDGE,"E14.MirrorCS"),sQuery(id+"F0.wireOp",EDGE,"E15.trimOffspring"),sQuery(id+"F0.wireOp",EDGE,"E16"),sQuery(id+"F0.wireOp",EDGE,"E17"),sQuery(id+"F0.wireOp",EDGE,"E18.1.0"),sQuery(id+"F0.wireOp",EDGE,"E18.1.1"),sQuery(id+"F0.wireOp",EDGE,"E18.1.2"),sQuery(id+"F0.wireOp",EDGE,"E18.1.3"),sQuery(id+"F0.wireOp",EDGE,"E18.1.4"),sQuery(id+"F0.wireOp",EDGE,"E18.1.5"),sQuery(id+"F0.wireOp",EDGE,"E18.1.6"),sQuery(id+"F0.wireOp",EDGE,"E18.1.7"),sQuery(id+"F0.wireOp",EDGE,"E18.1.8"),sQuery(id+"F0.wireOp",EDGE,"E18.1.9"),sQuery(id+"F0.wireOp",EDGE,"E18.1.10"),sQuery(id+"F0.wireOp",EDGE,"E18.1.11"),sQuery(id+"F0.wireOp",EDGE,"E18.1.12"),sQuery(id+"F0.wireOp",EDGE,"E18.1.13"),sQuery(id+"F0.wireOp",EDGE,"E18.1.14"),sQuery(id+"F0.wireOp",EDGE,"E18.1.15"),sQuery(id+"F0.wireOp",EDGE,"E18.2.0"),sQuery(id+"F0.wireOp",EDGE,"E18.2.1"),sQuery(id+"F0.wireOp",EDGE,"E18.2.2"),sQuery(id+"F0.wireOp",EDGE,"E18.2.3"),sQuery(id+"F0.wireOp",EDGE,"E18.2.4"),sQuery(id+"F0.wireOp",EDGE,"E18.2.5"),sQuery(id+"F0.wireOp",EDGE,"E18.2.6"),sQuery(id+"F0.wireOp",EDGE,"E18.2.7"),sQuery(id+"F0.wireOp",EDGE,"E18.2.8"),sQuery(id+"F0.wireOp",EDGE,"E18.2.9"),sQuery(id+"F0.wireOp",EDGE,"E18.2.10"),sQuery(id+"F0.wireOp",EDGE,"E18.2.11"),sQuery(id+"F0.wireOp",EDGE,"E18.2.12"),sQuery(id+"F0.wireOp",EDGE,"E18.2.13"),sQuery(id+"F0.wireOp",EDGE,"E18.2.14"),sQuery(id+"F0.wireOp",EDGE,"E18.2.15"),sQuery(id+"F0.wireOp",EDGE,"E19"),sQuery(id+"F0.wireOp",EDGE,"E20"),sQuery(id+"F0.wireOp",EDGE,"E21"),sQuery(id+"F0.wireOp",EDGE,"E22")])],"isStart":false}),makeQuery(id+"F4.opExtrude","SWEPT_FACE",FACE,{"disambiguationData":[OSD([sQuery(id+"F3.wireOp",EDGE,"E34")])]})]});
            var Q5;
            Q5=makeQuery(id+"F4.boolean.opBoolean","INTERSECT",EDGE,{"derivedFrom":[makeQuery(id+"F1.opExtrude","CAP_FACE",FACE,{"disambiguationData":[OSD([sQuery(id+"F0.wireOp",EDGE,"E0"),sQuery(id+"F0.wireOp",EDGE,"E1.2"),sQuery(id+"F0.wireOp",EDGE,"E1.3"),sQuery(id+"F0.wireOp",EDGE,"E1.4"),sQuery(id+"F0.wireOp",EDGE,"E4"),sQuery(id+"F0.wireOp",EDGE,"E5"),sQuery(id+"F0.wireOp",EDGE,"E6.0"),sQuery(id+"F0.wireOp",EDGE,"E6.1"),sQuery(id+"F0.wireOp",EDGE,"E7.filletArc"),sQuery(id+"F0.wireOp",EDGE,"E8.filletArc"),sQuery(id+"F0.wireOp",EDGE,"E10.MirrorCS"),sQuery(id+"F0.wireOp",EDGE,"E11.MirrorCS"),sQuery(id+"F0.wireOp",EDGE,"E12.MirrorCS"),sQuery(id+"F0.wireOp",EDGE,"E13.MirrorCS"),sQuery(id+"F0.wireOp",EDGE,"E14.MirrorCS"),sQuery(id+"F0.wireOp",EDGE,"E15.trimOffspring"),sQuery(id+"F0.wireOp",EDGE,"E16"),sQuery(id+"F0.wireOp",EDGE,"E17"),sQuery(id+"F0.wireOp",EDGE,"E18.1.0"),sQuery(id+"F0.wireOp",EDGE,"E18.1.1"),sQuery(id+"F0.wireOp",EDGE,"E18.1.2"),sQuery(id+"F0.wireOp",EDGE,"E18.1.3"),sQuery(id+"F0.wireOp",EDGE,"E18.1.4"),sQuery(id+"F0.wireOp",EDGE,"E18.1.5"),sQuery(id+"F0.wireOp",EDGE,"E18.1.6"),sQuery(id+"F0.wireOp",EDGE,"E18.1.7"),sQuery(id+"F0.wireOp",EDGE,"E18.1.8"),sQuery(id+"F0.wireOp",EDGE,"E18.1.9"),sQuery(id+"F0.wireOp",EDGE,"E18.1.10"),sQuery(id+"F0.wireOp",EDGE,"E18.1.11"),sQuery(id+"F0.wireOp",EDGE,"E18.1.12"),sQuery(id+"F0.wireOp",EDGE,"E18.1.13"),sQuery(id+"F0.wireOp",EDGE,"E18.1.14"),sQuery(id+"F0.wireOp",EDGE,"E18.1.15"),sQuery(id+"F0.wireOp",EDGE,"E18.2.0"),sQuery(id+"F0.wireOp",EDGE,"E18.2.1"),sQuery(id+"F0.wireOp",EDGE,"E18.2.2"),sQuery(id+"F0.wireOp",EDGE,"E18.2.3"),sQuery(id+"F0.wireOp",EDGE,"E18.2.4"),sQuery(id+"F0.wireOp",EDGE,"E18.2.5"),sQuery(id+"F0.wireOp",EDGE,"E18.2.6"),sQuery(id+"F0.wireOp",EDGE,"E18.2.7"),sQuery(id+"F0.wireOp",EDGE,"E18.2.8"),sQuery(id+"F0.wireOp",EDGE,"E18.2.9"),sQuery(id+"F0.wireOp",EDGE,"E18.2.10"),sQuery(id+"F0.wireOp",EDGE,"E18.2.11"),sQuery(id+"F0.wireOp",EDGE,"E18.2.12"),sQuery(id+"F0.wireOp",EDGE,"E18.2.13"),sQuery(id+"F0.wireOp",EDGE,"E18.2.14"),sQuery(id+"F0.wireOp",EDGE,"E18.2.15"),sQuery(id+"F0.wireOp",EDGE,"E19"),sQuery(id+"F0.wireOp",EDGE,"E20"),sQuery(id+"F0.wireOp",EDGE,"E21"),sQuery(id+"F0.wireOp",EDGE,"E22")])],"isStart":false}),makeQuery(id+"F4.opExtrude","SWEPT_FACE",FACE,{"disambiguationData":[OSD([sQuery(id+"F3.wireOp",EDGE,"E37.2.3")])]})]});
            fillet(context, id + "F8", {"entities" : qUnion([Q0, Q1, Q2, Q3, Q4, Q5]), "radius" : 5 * mm, "tangentPropagation" : true, "allowEdgeOverflow" : false});
        }
        {
            var Q0;
            {var subQ2=sQuery(id+"F5.wireOp",EDGE,"E42.2.1");var subQ3=sQuery(id+"F3.wireOp",EDGE,"E37.1.5");var subQ4=makeQuery(id+"F6.opExtrude","SWEPT_FACE",FACE,{"disambiguationData":[OSD([subQ2])]});var subQ5=sQuery(id+"F3.wireOp",EDGE,"E37.1.4");var subQ6=sQuery(id+"F0.wireOp",EDGE,"E18.2.4");var subQ7=sQuery(id+"F3.wireOp",EDGE,"E37.1.16");var subQ8=makeQuery(id+"F4.opExtrude","CAP_FACE",FACE,{"disambiguationData":[OSD([sQuery(id+"F3.wireOp",EDGE,"E37.1.1"),sQuery(id+"F3.wireOp",EDGE,"E37.1.2"),sQuery(id+"F3.wireOp",EDGE,"E37.1.3"),subQ5,subQ3,sQuery(id+"F3.wireOp",EDGE,"E37.1.6"),sQuery(id+"F3.wireOp",EDGE,"E37.1.7"),sQuery(id+"F3.wireOp",EDGE,"E37.1.8"),sQuery(id+"F3.wireOp",EDGE,"E37.1.9"),sQuery(id+"F3.wireOp",EDGE,"E37.1.10"),sQuery(id+"F3.wireOp",EDGE,"E37.1.11"),sQuery(id+"F3.wireOp",EDGE,"E37.1.12"),sQuery(id+"F3.wireOp",EDGE,"E37.1.13"),sQuery(id+"F3.wireOp",EDGE,"E37.1.14"),sQuery(id+"F3.wireOp",EDGE,"E37.1.15"),subQ7,sQuery(id+"F3.wireOp",EDGE,"E37.1.17"),sQuery(id+"F3.wireOp",EDGE,"E37.1.18")])],"isStart":false});Q0=makeQuery(id+"F7.boolean.opBoolean","SPLIT",EDGE,{"disambiguationData":[topologyDisambiguationEdgeConnected([subQ8,subQ4]),TD([makeQuery(id+"F1.opExtrude","SWEPT_FACE",FACE,{"disambiguationData":[OSD([subQ6])]})])],"derivedFrom":makeQuery(id+"F6.opExtrude","CAP_EDGE",EDGE,{"disambiguationData":[OSD([subQ2])],"isStart":true})});}
            var Q1;
            {var subQ0=sQuery(id+"F5.wireOp",EDGE,"E42.2.1");var subQ1=makeQuery(id+"F6.opExtrude","SWEPT_FACE",FACE,{"disambiguationData":[OSD([subQ0])]});var subQ2=sQuery(id+"F3.wireOp",EDGE,"E37.1.11");var subQ3=sQuery(id+"F3.wireOp",EDGE,"E37.1.6");var subQ5=sQuery(id+"F0.wireOp",EDGE,"E18.2.2");var subQ7=sQuery(id+"F3.wireOp",EDGE,"E37.1.1");var subQ8=makeQuery(id+"F4.opExtrude","CAP_FACE",FACE,{"disambiguationData":[OSD([subQ7,sQuery(id+"F3.wireOp",EDGE,"E37.1.2"),sQuery(id+"F3.wireOp",EDGE,"E37.1.3"),sQuery(id+"F3.wireOp",EDGE,"E37.1.4"),sQuery(id+"F3.wireOp",EDGE,"E37.1.5"),subQ3,sQuery(id+"F3.wireOp",EDGE,"E37.1.7"),sQuery(id+"F3.wireOp",EDGE,"E37.1.8"),sQuery(id+"F3.wireOp",EDGE,"E37.1.9"),sQuery(id+"F3.wireOp",EDGE,"E37.1.10"),subQ2,sQuery(id+"F3.wireOp",EDGE,"E37.1.12"),sQuery(id+"F3.wireOp",EDGE,"E37.1.13"),sQuery(id+"F3.wireOp",EDGE,"E37.1.14"),sQuery(id+"F3.wireOp",EDGE,"E37.1.15"),sQuery(id+"F3.wireOp",EDGE,"E37.1.16"),sQuery(id+"F3.wireOp",EDGE,"E37.1.17"),sQuery(id+"F3.wireOp",EDGE,"E37.1.18")])],"isStart":false});Q1=makeQuery(id+"F7.boolean.opBoolean","SPLIT",EDGE,{"disambiguationData":[topologyDisambiguationEdgeConnected([subQ8,subQ1]),TD([makeQuery(id+"F1.opExtrude","SWEPT_FACE",FACE,{"disambiguationData":[OSD([subQ5])]})])],"derivedFrom":makeQuery(id+"F6.opExtrude","CAP_EDGE",EDGE,{"disambiguationData":[OSD([subQ0])],"isStart":true})});}
            var Q2;
            {var subQ1=sQuery(id+"F5.wireOp",EDGE,"E42.2.1");var subQ2=sQuery(id+"F3.wireOp",EDGE,"E37.1.4");var subQ3=sQuery(id+"F0.wireOp",EDGE,"E18.2.4");var subQ4=makeQuery(id+"F7.opPattern","COPY",FACE,{"derivedFrom":makeQuery(id+"F6.opExtrude","SWEPT_FACE",FACE,{"disambiguationData":[OSD([subQ1])]}),"instanceName":"1"});var subQ6=sQuery(id+"F3.wireOp",EDGE,"E37.1.16");var subQ7=sQuery(id+"F3.wireOp",EDGE,"E37.1.5");var subQ8=makeQuery(id+"F4.opExtrude","CAP_FACE",FACE,{"disambiguationData":[OSD([sQuery(id+"F3.wireOp",EDGE,"E37.1.1"),sQuery(id+"F3.wireOp",EDGE,"E37.1.2"),sQuery(id+"F3.wireOp",EDGE,"E37.1.3"),subQ2,subQ7,sQuery(id+"F3.wireOp",EDGE,"E37.1.6"),sQuery(id+"F3.wireOp",EDGE,"E37.1.7"),sQuery(id+"F3.wireOp",EDGE,"E37.1.8"),sQuery(id+"F3.wireOp",EDGE,"E37.1.9"),sQuery(id+"F3.wireOp",EDGE,"E37.1.10"),sQuery(id+"F3.wireOp",EDGE,"E37.1.11"),sQuery(id+"F3.wireOp",EDGE,"E37.1.12"),sQuery(id+"F3.wireOp",EDGE,"E37.1.13"),sQuery(id+"F3.wireOp",EDGE,"E37.1.14"),sQuery(id+"F3.wireOp",EDGE,"E37.1.15"),subQ6,sQuery(id+"F3.wireOp",EDGE,"E37.1.17"),sQuery(id+"F3.wireOp",EDGE,"E37.1.18")])],"isStart":true});Q2=makeQuery(id+"F7.boolean.opBoolean","SPLIT",EDGE,{"disambiguationData":[topologyDisambiguationEdgeConnected([subQ8,subQ4]),TD([makeQuery(id+"F1.opExtrude","SWEPT_FACE",FACE,{"disambiguationData":[OSD([subQ3])]})])],"derivedFrom":makeQuery(id+"F7.opPattern","COPY",EDGE,{"derivedFrom":makeQuery(id+"F6.opExtrude","CAP_EDGE",EDGE,{"disambiguationData":[OSD([subQ1])],"isStart":true}),"instanceName":"1"})});}
            var Q3;
            {var subQ0=sQuery(id+"F3.wireOp",EDGE,"E37.1.6");var subQ1=sQuery(id+"F5.wireOp",EDGE,"E42.2.1");var subQ2=makeQuery(id+"F7.opPattern","COPY",FACE,{"derivedFrom":makeQuery(id+"F6.opExtrude","SWEPT_FACE",FACE,{"disambiguationData":[OSD([subQ1])]}),"instanceName":"1"});var subQ3=sQuery(id+"F3.wireOp",EDGE,"E37.1.11");var subQ4=sQuery(id+"F3.wireOp",EDGE,"E37.1.1");var subQ5=makeQuery(id+"F4.opExtrude","CAP_FACE",FACE,{"disambiguationData":[OSD([subQ4,sQuery(id+"F3.wireOp",EDGE,"E37.1.2"),sQuery(id+"F3.wireOp",EDGE,"E37.1.3"),sQuery(id+"F3.wireOp",EDGE,"E37.1.4"),sQuery(id+"F3.wireOp",EDGE,"E37.1.5"),subQ0,sQuery(id+"F3.wireOp",EDGE,"E37.1.7"),sQuery(id+"F3.wireOp",EDGE,"E37.1.8"),sQuery(id+"F3.wireOp",EDGE,"E37.1.9"),sQuery(id+"F3.wireOp",EDGE,"E37.1.10"),subQ3,sQuery(id+"F3.wireOp",EDGE,"E37.1.12"),sQuery(id+"F3.wireOp",EDGE,"E37.1.13"),sQuery(id+"F3.wireOp",EDGE,"E37.1.14"),sQuery(id+"F3.wireOp",EDGE,"E37.1.15"),sQuery(id+"F3.wireOp",EDGE,"E37.1.16"),sQuery(id+"F3.wireOp",EDGE,"E37.1.17"),sQuery(id+"F3.wireOp",EDGE,"E37.1.18")])],"isStart":true});var subQ6=sQuery(id+"F0.wireOp",EDGE,"E18.2.2");Q3=makeQuery(id+"F7.boolean.opBoolean","SPLIT",EDGE,{"disambiguationData":[topologyDisambiguationEdgeConnected([subQ5,subQ2]),TD([makeQuery(id+"F1.opExtrude","SWEPT_FACE",FACE,{"disambiguationData":[OSD([subQ6])]})])],"derivedFrom":makeQuery(id+"F7.opPattern","COPY",EDGE,{"derivedFrom":makeQuery(id+"F6.opExtrude","CAP_EDGE",EDGE,{"disambiguationData":[OSD([subQ1])],"isStart":true}),"instanceName":"1"})});}
            var Q4;
            {var subQ2=sQuery(id+"F5.wireOp",EDGE,"E39");var subQ3=sQuery(id+"F3.wireOp",EDGE,"E33.0");var subQ4=sQuery(id+"F3.wireOp",EDGE,"E25.MirrorCS");var subQ6=makeQuery(id+"F6.opExtrude","SWEPT_FACE",FACE,{"disambiguationData":[OSD([subQ2])]});var subQ7=sQuery(id+"F3.wireOp",EDGE,"E26.MirrorCS");var subQ8=makeQuery(id+"F4.opExtrude","CAP_FACE",FACE,{"disambiguationData":[OSD([sQuery(id+"F3.wireOp",EDGE,"E23.0"),sQuery(id+"F3.wireOp",EDGE,"E23.1"),sQuery(id+"F3.wireOp",EDGE,"E23.2"),sQuery(id+"F3.wireOp",EDGE,"E23.3"),sQuery(id+"F3.wireOp",EDGE,"E23.4"),sQuery(id+"F3.wireOp",EDGE,"E23.5"),sQuery(id+"F3.wireOp",EDGE,"E23.6"),subQ4,subQ7,sQuery(id+"F3.wireOp",EDGE,"E27.MirrorCS"),sQuery(id+"F3.wireOp",EDGE,"E28.MirrorCS"),sQuery(id+"F3.wireOp",EDGE,"E29.MirrorCS"),sQuery(id+"F3.wireOp",EDGE,"E30.MirrorCS"),sQuery(id+"F3.wireOp",EDGE,"E31.MirrorCS"),sQuery(id+"F3.wireOp",EDGE,"E32"),subQ3,sQuery(id+"F3.wireOp",EDGE,"E33.1"),sQuery(id+"F3.wireOp",EDGE,"E34")])],"isStart":false});Q4=makeQuery(id+"F7.boolean.opBoolean","SPLIT",EDGE,{"disambiguationData":[topologyDisambiguationEdgeConnected([subQ8,subQ6]),TD([makeQuery(id+"F1.opExtrude","SWEPT_FACE",FACE,{"disambiguationData":[OSD([sQuery(id+"F0.wireOp",EDGE,"E1.2")])]})])],"derivedFrom":makeQuery(id+"F6.opExtrude","CAP_EDGE",EDGE,{"disambiguationData":[OSD([subQ2])],"isStart":true})});}
            var Q5;
            {var subQ0=sQuery(id+"F5.wireOp",EDGE,"E39");var subQ1=makeQuery(id+"F6.opExtrude","SWEPT_FACE",FACE,{"disambiguationData":[OSD([subQ0])]});var subQ2=sQuery(id+"F3.wireOp",EDGE,"E33.1");var subQ5=sQuery(id+"F3.wireOp",EDGE,"E23.3");var subQ6=sQuery(id+"F3.wireOp",EDGE,"E23.2");var subQ8=makeQuery(id+"F4.opExtrude","CAP_FACE",FACE,{"disambiguationData":[OSD([sQuery(id+"F3.wireOp",EDGE,"E23.0"),sQuery(id+"F3.wireOp",EDGE,"E23.1"),subQ6,subQ5,sQuery(id+"F3.wireOp",EDGE,"E23.4"),sQuery(id+"F3.wireOp",EDGE,"E23.5"),sQuery(id+"F3.wireOp",EDGE,"E23.6"),sQuery(id+"F3.wireOp",EDGE,"E25.MirrorCS"),sQuery(id+"F3.wireOp",EDGE,"E26.MirrorCS"),sQuery(id+"F3.wireOp",EDGE,"E27.MirrorCS"),sQuery(id+"F3.wireOp",EDGE,"E28.MirrorCS"),sQuery(id+"F3.wireOp",EDGE,"E29.MirrorCS"),sQuery(id+"F3.wireOp",EDGE,"E30.MirrorCS"),sQuery(id+"F3.wireOp",EDGE,"E31.MirrorCS"),sQuery(id+"F3.wireOp",EDGE,"E32"),sQuery(id+"F3.wireOp",EDGE,"E33.0"),subQ2,sQuery(id+"F3.wireOp",EDGE,"E34")])],"isStart":false});Q5=makeQuery(id+"F7.boolean.opBoolean","SPLIT",EDGE,{"disambiguationData":[topologyDisambiguationEdgeConnected([subQ8,subQ1]),TD([makeQuery(id+"F1.opExtrude","SWEPT_FACE",FACE,{"disambiguationData":[OSD([sQuery(id+"F0.wireOp",EDGE,"E1.4")])]})])],"derivedFrom":makeQuery(id+"F6.opExtrude","CAP_EDGE",EDGE,{"disambiguationData":[OSD([subQ0])],"isStart":true})});}
            var Q6;
            {var subQ2=sQuery(id+"F3.wireOp",EDGE,"E33.0");var subQ3=sQuery(id+"F3.wireOp",EDGE,"E25.MirrorCS");var subQ5=sQuery(id+"F5.wireOp",EDGE,"E39");var subQ6=sQuery(id+"F3.wireOp",EDGE,"E26.MirrorCS");var subQ7=makeQuery(id+"F4.opExtrude","CAP_FACE",FACE,{"disambiguationData":[OSD([sQuery(id+"F3.wireOp",EDGE,"E23.0"),sQuery(id+"F3.wireOp",EDGE,"E23.1"),sQuery(id+"F3.wireOp",EDGE,"E23.2"),sQuery(id+"F3.wireOp",EDGE,"E23.3"),sQuery(id+"F3.wireOp",EDGE,"E23.4"),sQuery(id+"F3.wireOp",EDGE,"E23.5"),sQuery(id+"F3.wireOp",EDGE,"E23.6"),subQ3,subQ6,sQuery(id+"F3.wireOp",EDGE,"E27.MirrorCS"),sQuery(id+"F3.wireOp",EDGE,"E28.MirrorCS"),sQuery(id+"F3.wireOp",EDGE,"E29.MirrorCS"),sQuery(id+"F3.wireOp",EDGE,"E30.MirrorCS"),sQuery(id+"F3.wireOp",EDGE,"E31.MirrorCS"),sQuery(id+"F3.wireOp",EDGE,"E32"),subQ2,sQuery(id+"F3.wireOp",EDGE,"E33.1"),sQuery(id+"F3.wireOp",EDGE,"E34")])],"isStart":true});var subQ8=makeQuery(id+"F7.opPattern","COPY",FACE,{"derivedFrom":makeQuery(id+"F6.opExtrude","SWEPT_FACE",FACE,{"disambiguationData":[OSD([subQ5])]}),"instanceName":"1"});Q6=makeQuery(id+"F7.boolean.opBoolean","SPLIT",EDGE,{"disambiguationData":[topologyDisambiguationEdgeConnected([subQ7,subQ8]),TD([makeQuery(id+"F1.opExtrude","SWEPT_FACE",FACE,{"disambiguationData":[OSD([sQuery(id+"F0.wireOp",EDGE,"E1.2")])]})])],"derivedFrom":makeQuery(id+"F7.opPattern","COPY",EDGE,{"derivedFrom":makeQuery(id+"F6.opExtrude","CAP_EDGE",EDGE,{"disambiguationData":[OSD([subQ5])],"isStart":true}),"instanceName":"1"})});}
            var Q7;
            {var subQ2=sQuery(id+"F5.wireOp",EDGE,"E39");var subQ3=sQuery(id+"F3.wireOp",EDGE,"E33.1");var subQ4=sQuery(id+"F3.wireOp",EDGE,"E23.3");var subQ5=sQuery(id+"F3.wireOp",EDGE,"E23.2");var subQ6=makeQuery(id+"F4.opExtrude","CAP_FACE",FACE,{"disambiguationData":[OSD([sQuery(id+"F3.wireOp",EDGE,"E23.0"),sQuery(id+"F3.wireOp",EDGE,"E23.1"),subQ5,subQ4,sQuery(id+"F3.wireOp",EDGE,"E23.4"),sQuery(id+"F3.wireOp",EDGE,"E23.5"),sQuery(id+"F3.wireOp",EDGE,"E23.6"),sQuery(id+"F3.wireOp",EDGE,"E25.MirrorCS"),sQuery(id+"F3.wireOp",EDGE,"E26.MirrorCS"),sQuery(id+"F3.wireOp",EDGE,"E27.MirrorCS"),sQuery(id+"F3.wireOp",EDGE,"E28.MirrorCS"),sQuery(id+"F3.wireOp",EDGE,"E29.MirrorCS"),sQuery(id+"F3.wireOp",EDGE,"E30.MirrorCS"),sQuery(id+"F3.wireOp",EDGE,"E31.MirrorCS"),sQuery(id+"F3.wireOp",EDGE,"E32"),sQuery(id+"F3.wireOp",EDGE,"E33.0"),subQ3,sQuery(id+"F3.wireOp",EDGE,"E34")])],"isStart":true});var subQ7=makeQuery(id+"F7.opPattern","COPY",FACE,{"derivedFrom":makeQuery(id+"F6.opExtrude","SWEPT_FACE",FACE,{"disambiguationData":[OSD([subQ2])]}),"instanceName":"1"});Q7=makeQuery(id+"F7.boolean.opBoolean","SPLIT",EDGE,{"disambiguationData":[topologyDisambiguationEdgeConnected([subQ6,subQ7]),TD([makeQuery(id+"F1.opExtrude","SWEPT_FACE",FACE,{"disambiguationData":[OSD([sQuery(id+"F0.wireOp",EDGE,"E1.4")])]})])],"derivedFrom":makeQuery(id+"F7.opPattern","COPY",EDGE,{"derivedFrom":makeQuery(id+"F6.opExtrude","CAP_EDGE",EDGE,{"disambiguationData":[OSD([subQ2])],"isStart":true}),"instanceName":"1"})});}
            var Q8;
            {var subQ2=sQuery(id+"F3.wireOp",EDGE,"E37.2.5");var subQ3=sQuery(id+"F5.wireOp",EDGE,"E42.1.1");var subQ4=makeQuery(id+"F6.opExtrude","SWEPT_FACE",FACE,{"disambiguationData":[OSD([subQ3])]});var subQ5=sQuery(id+"F3.wireOp",EDGE,"E37.2.16");var subQ6=sQuery(id+"F3.wireOp",EDGE,"E37.2.4");var subQ7=makeQuery(id+"F4.opExtrude","CAP_FACE",FACE,{"disambiguationData":[OSD([sQuery(id+"F3.wireOp",EDGE,"E37.2.1"),sQuery(id+"F3.wireOp",EDGE,"E37.2.2"),sQuery(id+"F3.wireOp",EDGE,"E37.2.3"),subQ6,subQ2,sQuery(id+"F3.wireOp",EDGE,"E37.2.6"),sQuery(id+"F3.wireOp",EDGE,"E37.2.7"),sQuery(id+"F3.wireOp",EDGE,"E37.2.8"),sQuery(id+"F3.wireOp",EDGE,"E37.2.9"),sQuery(id+"F3.wireOp",EDGE,"E37.2.10"),sQuery(id+"F3.wireOp",EDGE,"E37.2.11"),sQuery(id+"F3.wireOp",EDGE,"E37.2.12"),sQuery(id+"F3.wireOp",EDGE,"E37.2.13"),sQuery(id+"F3.wireOp",EDGE,"E37.2.14"),sQuery(id+"F3.wireOp",EDGE,"E37.2.15"),subQ5,sQuery(id+"F3.wireOp",EDGE,"E37.2.17"),sQuery(id+"F3.wireOp",EDGE,"E37.2.18")])],"isStart":false});var subQ8=sQuery(id+"F0.wireOp",EDGE,"E18.1.4");Q8=makeQuery(id+"F7.boolean.opBoolean","SPLIT",EDGE,{"disambiguationData":[topologyDisambiguationEdgeConnected([subQ7,subQ4]),TD([makeQuery(id+"F1.opExtrude","SWEPT_FACE",FACE,{"disambiguationData":[OSD([subQ8])]})])],"derivedFrom":makeQuery(id+"F6.opExtrude","CAP_EDGE",EDGE,{"disambiguationData":[OSD([subQ3])],"isStart":true})});}
            var Q9;
            {var subQ0=sQuery(id+"F5.wireOp",EDGE,"E42.1.1");var subQ1=makeQuery(id+"F6.opExtrude","SWEPT_FACE",FACE,{"disambiguationData":[OSD([subQ0])]});var subQ2=sQuery(id+"F3.wireOp",EDGE,"E37.2.11");var subQ3=sQuery(id+"F3.wireOp",EDGE,"E37.2.6");var subQ4=sQuery(id+"F3.wireOp",EDGE,"E37.2.1");var subQ5=makeQuery(id+"F4.opExtrude","CAP_FACE",FACE,{"disambiguationData":[OSD([subQ4,sQuery(id+"F3.wireOp",EDGE,"E37.2.2"),sQuery(id+"F3.wireOp",EDGE,"E37.2.3"),sQuery(id+"F3.wireOp",EDGE,"E37.2.4"),sQuery(id+"F3.wireOp",EDGE,"E37.2.5"),subQ3,sQuery(id+"F3.wireOp",EDGE,"E37.2.7"),sQuery(id+"F3.wireOp",EDGE,"E37.2.8"),sQuery(id+"F3.wireOp",EDGE,"E37.2.9"),sQuery(id+"F3.wireOp",EDGE,"E37.2.10"),subQ2,sQuery(id+"F3.wireOp",EDGE,"E37.2.12"),sQuery(id+"F3.wireOp",EDGE,"E37.2.13"),sQuery(id+"F3.wireOp",EDGE,"E37.2.14"),sQuery(id+"F3.wireOp",EDGE,"E37.2.15"),sQuery(id+"F3.wireOp",EDGE,"E37.2.16"),sQuery(id+"F3.wireOp",EDGE,"E37.2.17"),sQuery(id+"F3.wireOp",EDGE,"E37.2.18")])],"isStart":false});var subQ8=sQuery(id+"F0.wireOp",EDGE,"E18.1.2");Q9=makeQuery(id+"F7.boolean.opBoolean","SPLIT",EDGE,{"disambiguationData":[topologyDisambiguationEdgeConnected([subQ5,subQ1]),TD([makeQuery(id+"F1.opExtrude","SWEPT_FACE",FACE,{"disambiguationData":[OSD([subQ8])]})])],"derivedFrom":makeQuery(id+"F6.opExtrude","CAP_EDGE",EDGE,{"disambiguationData":[OSD([subQ0])],"isStart":true})});}
            var Q10;
            {var subQ1=sQuery(id+"F5.wireOp",EDGE,"E42.1.1");var subQ2=makeQuery(id+"F7.opPattern","COPY",FACE,{"derivedFrom":makeQuery(id+"F6.opExtrude","SWEPT_FACE",FACE,{"disambiguationData":[OSD([subQ1])]}),"instanceName":"1"});var subQ4=sQuery(id+"F3.wireOp",EDGE,"E37.2.5");var subQ5=sQuery(id+"F3.wireOp",EDGE,"E37.2.4");var subQ6=sQuery(id+"F0.wireOp",EDGE,"E18.1.4");var subQ7=sQuery(id+"F3.wireOp",EDGE,"E37.2.16");var subQ8=makeQuery(id+"F4.opExtrude","CAP_FACE",FACE,{"disambiguationData":[OSD([sQuery(id+"F3.wireOp",EDGE,"E37.2.1"),sQuery(id+"F3.wireOp",EDGE,"E37.2.2"),sQuery(id+"F3.wireOp",EDGE,"E37.2.3"),subQ5,subQ4,sQuery(id+"F3.wireOp",EDGE,"E37.2.6"),sQuery(id+"F3.wireOp",EDGE,"E37.2.7"),sQuery(id+"F3.wireOp",EDGE,"E37.2.8"),sQuery(id+"F3.wireOp",EDGE,"E37.2.9"),sQuery(id+"F3.wireOp",EDGE,"E37.2.10"),sQuery(id+"F3.wireOp",EDGE,"E37.2.11"),sQuery(id+"F3.wireOp",EDGE,"E37.2.12"),sQuery(id+"F3.wireOp",EDGE,"E37.2.13"),sQuery(id+"F3.wireOp",EDGE,"E37.2.14"),sQuery(id+"F3.wireOp",EDGE,"E37.2.15"),subQ7,sQuery(id+"F3.wireOp",EDGE,"E37.2.17"),sQuery(id+"F3.wireOp",EDGE,"E37.2.18")])],"isStart":true});Q10=makeQuery(id+"F7.boolean.opBoolean","SPLIT",EDGE,{"disambiguationData":[topologyDisambiguationEdgeConnected([subQ8,subQ2]),TD([makeQuery(id+"F1.opExtrude","SWEPT_FACE",FACE,{"disambiguationData":[OSD([subQ6])]})])],"derivedFrom":makeQuery(id+"F7.opPattern","COPY",EDGE,{"derivedFrom":makeQuery(id+"F6.opExtrude","CAP_EDGE",EDGE,{"disambiguationData":[OSD([subQ1])],"isStart":true}),"instanceName":"1"})});}
            var Q11;
            {var subQ0=sQuery(id+"F5.wireOp",EDGE,"E42.1.1");var subQ1=makeQuery(id+"F7.opPattern","COPY",FACE,{"derivedFrom":makeQuery(id+"F6.opExtrude","SWEPT_FACE",FACE,{"disambiguationData":[OSD([subQ0])]}),"instanceName":"1"});var subQ4=sQuery(id+"F3.wireOp",EDGE,"E37.2.6");var subQ5=sQuery(id+"F3.wireOp",EDGE,"E37.2.11");var subQ6=sQuery(id+"F3.wireOp",EDGE,"E37.2.1");var subQ7=makeQuery(id+"F4.opExtrude","CAP_FACE",FACE,{"disambiguationData":[OSD([subQ6,sQuery(id+"F3.wireOp",EDGE,"E37.2.2"),sQuery(id+"F3.wireOp",EDGE,"E37.2.3"),sQuery(id+"F3.wireOp",EDGE,"E37.2.4"),sQuery(id+"F3.wireOp",EDGE,"E37.2.5"),subQ4,sQuery(id+"F3.wireOp",EDGE,"E37.2.7"),sQuery(id+"F3.wireOp",EDGE,"E37.2.8"),sQuery(id+"F3.wireOp",EDGE,"E37.2.9"),sQuery(id+"F3.wireOp",EDGE,"E37.2.10"),subQ5,sQuery(id+"F3.wireOp",EDGE,"E37.2.12"),sQuery(id+"F3.wireOp",EDGE,"E37.2.13"),sQuery(id+"F3.wireOp",EDGE,"E37.2.14"),sQuery(id+"F3.wireOp",EDGE,"E37.2.15"),sQuery(id+"F3.wireOp",EDGE,"E37.2.16"),sQuery(id+"F3.wireOp",EDGE,"E37.2.17"),sQuery(id+"F3.wireOp",EDGE,"E37.2.18")])],"isStart":true});var subQ8=sQuery(id+"F0.wireOp",EDGE,"E18.1.2");Q11=makeQuery(id+"F7.boolean.opBoolean","SPLIT",EDGE,{"disambiguationData":[topologyDisambiguationEdgeConnected([subQ7,subQ1]),TD([makeQuery(id+"F1.opExtrude","SWEPT_FACE",FACE,{"disambiguationData":[OSD([subQ8])]})])],"derivedFrom":makeQuery(id+"F7.opPattern","COPY",EDGE,{"derivedFrom":makeQuery(id+"F6.opExtrude","CAP_EDGE",EDGE,{"disambiguationData":[OSD([subQ0])],"isStart":true}),"instanceName":"1"})});}
            var Q12;
            Q12=makeQuery(id+"F8.opFillet","BLEND_EDGE",EDGE,{"blendedFrom":[makeQuery(id+"F4.boolean.opBoolean","INTERSECT",EDGE,{"derivedFrom":[makeQuery(id+"F1.opExtrude","CAP_FACE",FACE,{"disambiguationData":[OSD([sQuery(id+"F0.wireOp",EDGE,"E0"),sQuery(id+"F0.wireOp",EDGE,"E1.2"),sQuery(id+"F0.wireOp",EDGE,"E1.3"),sQuery(id+"F0.wireOp",EDGE,"E1.4"),sQuery(id+"F0.wireOp",EDGE,"E4"),sQuery(id+"F0.wireOp",EDGE,"E5"),sQuery(id+"F0.wireOp",EDGE,"E6.0"),sQuery(id+"F0.wireOp",EDGE,"E6.1"),sQuery(id+"F0.wireOp",EDGE,"E7.filletArc"),sQuery(id+"F0.wireOp",EDGE,"E8.filletArc"),sQuery(id+"F0.wireOp",EDGE,"E10.MirrorCS"),sQuery(id+"F0.wireOp",EDGE,"E11.MirrorCS"),sQuery(id+"F0.wireOp",EDGE,"E12.MirrorCS"),sQuery(id+"F0.wireOp",EDGE,"E13.MirrorCS"),sQuery(id+"F0.wireOp",EDGE,"E14.MirrorCS"),sQuery(id+"F0.wireOp",EDGE,"E15.trimOffspring"),sQuery(id+"F0.wireOp",EDGE,"E16"),sQuery(id+"F0.wireOp",EDGE,"E17"),sQuery(id+"F0.wireOp",EDGE,"E18.1.0"),sQuery(id+"F0.wireOp",EDGE,"E18.1.1"),sQuery(id+"F0.wireOp",EDGE,"E18.1.2"),sQuery(id+"F0.wireOp",EDGE,"E18.1.3"),sQuery(id+"F0.wireOp",EDGE,"E18.1.4"),sQuery(id+"F0.wireOp",EDGE,"E18.1.5"),sQuery(id+"F0.wireOp",EDGE,"E18.1.6"),sQuery(id+"F0.wireOp",EDGE,"E18.1.7"),sQuery(id+"F0.wireOp",EDGE,"E18.1.8"),sQuery(id+"F0.wireOp",EDGE,"E18.1.9"),sQuery(id+"F0.wireOp",EDGE,"E18.1.10"),sQuery(id+"F0.wireOp",EDGE,"E18.1.11"),sQuery(id+"F0.wireOp",EDGE,"E18.1.12"),sQuery(id+"F0.wireOp",EDGE,"E18.1.13"),sQuery(id+"F0.wireOp",EDGE,"E18.1.14"),sQuery(id+"F0.wireOp",EDGE,"E18.1.15"),sQuery(id+"F0.wireOp",EDGE,"E18.2.0"),sQuery(id+"F0.wireOp",EDGE,"E18.2.1"),sQuery(id+"F0.wireOp",EDGE,"E18.2.2"),sQuery(id+"F0.wireOp",EDGE,"E18.2.3"),sQuery(id+"F0.wireOp",EDGE,"E18.2.4"),sQuery(id+"F0.wireOp",EDGE,"E18.2.5"),sQuery(id+"F0.wireOp",EDGE,"E18.2.6"),sQuery(id+"F0.wireOp",EDGE,"E18.2.7"),sQuery(id+"F0.wireOp",EDGE,"E18.2.8"),sQuery(id+"F0.wireOp",EDGE,"E18.2.9"),sQuery(id+"F0.wireOp",EDGE,"E18.2.10"),sQuery(id+"F0.wireOp",EDGE,"E18.2.11"),sQuery(id+"F0.wireOp",EDGE,"E18.2.12"),sQuery(id+"F0.wireOp",EDGE,"E18.2.13"),sQuery(id+"F0.wireOp",EDGE,"E18.2.14"),sQuery(id+"F0.wireOp",EDGE,"E18.2.15"),sQuery(id+"F0.wireOp",EDGE,"E19"),sQuery(id+"F0.wireOp",EDGE,"E20"),sQuery(id+"F0.wireOp",EDGE,"E21"),sQuery(id+"F0.wireOp",EDGE,"E22")])],"isStart":true}),makeQuery(id+"F4.opExtrude","SWEPT_FACE",FACE,{"disambiguationData":[OSD([sQuery(id+"F3.wireOp",EDGE,"E37.2.3")])]})]}),makeQuery(id+"F7.opPattern","COPY",FACE,{"derivedFrom":makeQuery(id+"F6.opExtrude","CAP_FACE",FACE,{"disambiguationData":[OSD([sQuery(id+"F5.wireOp",EDGE,"E42.1.1"),sQuery(id+"F5.wireOp",EDGE,"E42.1.3"),sQuery(id+"F5.wireOp",EDGE,"E42.1.4"),sQuery(id+"F5.wireOp",EDGE,"E42.1.5")])],"isStart":false}),"instanceName":"1"})],"blendedInto":[makeQuery(id+"F7.opPattern","COPY",FACE,{"derivedFrom":makeQuery(id+"F6.opExtrude","CAP_FACE",FACE,{"disambiguationData":[OSD([sQuery(id+"F5.wireOp",EDGE,"E42.1.1"),sQuery(id+"F5.wireOp",EDGE,"E42.1.3"),sQuery(id+"F5.wireOp",EDGE,"E42.1.4"),sQuery(id+"F5.wireOp",EDGE,"E42.1.5")])],"isStart":false}),"instanceName":"1"})]});
            var Q13;
            Q13=makeQuery(id+"F8.opFillet","BLEND_EDGE",EDGE,{"blendedFrom":[makeQuery(id+"F4.boolean.opBoolean","INTERSECT",EDGE,{"derivedFrom":[makeQuery(id+"F1.opExtrude","CAP_FACE",FACE,{"disambiguationData":[OSD([sQuery(id+"F0.wireOp",EDGE,"E0"),sQuery(id+"F0.wireOp",EDGE,"E1.2"),sQuery(id+"F0.wireOp",EDGE,"E1.3"),sQuery(id+"F0.wireOp",EDGE,"E1.4"),sQuery(id+"F0.wireOp",EDGE,"E4"),sQuery(id+"F0.wireOp",EDGE,"E5"),sQuery(id+"F0.wireOp",EDGE,"E6.0"),sQuery(id+"F0.wireOp",EDGE,"E6.1"),sQuery(id+"F0.wireOp",EDGE,"E7.filletArc"),sQuery(id+"F0.wireOp",EDGE,"E8.filletArc"),sQuery(id+"F0.wireOp",EDGE,"E10.MirrorCS"),sQuery(id+"F0.wireOp",EDGE,"E11.MirrorCS"),sQuery(id+"F0.wireOp",EDGE,"E12.MirrorCS"),sQuery(id+"F0.wireOp",EDGE,"E13.MirrorCS"),sQuery(id+"F0.wireOp",EDGE,"E14.MirrorCS"),sQuery(id+"F0.wireOp",EDGE,"E15.trimOffspring"),sQuery(id+"F0.wireOp",EDGE,"E16"),sQuery(id+"F0.wireOp",EDGE,"E17"),sQuery(id+"F0.wireOp",EDGE,"E18.1.0"),sQuery(id+"F0.wireOp",EDGE,"E18.1.1"),sQuery(id+"F0.wireOp",EDGE,"E18.1.2"),sQuery(id+"F0.wireOp",EDGE,"E18.1.3"),sQuery(id+"F0.wireOp",EDGE,"E18.1.4"),sQuery(id+"F0.wireOp",EDGE,"E18.1.5"),sQuery(id+"F0.wireOp",EDGE,"E18.1.6"),sQuery(id+"F0.wireOp",EDGE,"E18.1.7"),sQuery(id+"F0.wireOp",EDGE,"E18.1.8"),sQuery(id+"F0.wireOp",EDGE,"E18.1.9"),sQuery(id+"F0.wireOp",EDGE,"E18.1.10"),sQuery(id+"F0.wireOp",EDGE,"E18.1.11"),sQuery(id+"F0.wireOp",EDGE,"E18.1.12"),sQuery(id+"F0.wireOp",EDGE,"E18.1.13"),sQuery(id+"F0.wireOp",EDGE,"E18.1.14"),sQuery(id+"F0.wireOp",EDGE,"E18.1.15"),sQuery(id+"F0.wireOp",EDGE,"E18.2.0"),sQuery(id+"F0.wireOp",EDGE,"E18.2.1"),sQuery(id+"F0.wireOp",EDGE,"E18.2.2"),sQuery(id+"F0.wireOp",EDGE,"E18.2.3"),sQuery(id+"F0.wireOp",EDGE,"E18.2.4"),sQuery(id+"F0.wireOp",EDGE,"E18.2.5"),sQuery(id+"F0.wireOp",EDGE,"E18.2.6"),sQuery(id+"F0.wireOp",EDGE,"E18.2.7"),sQuery(id+"F0.wireOp",EDGE,"E18.2.8"),sQuery(id+"F0.wireOp",EDGE,"E18.2.9"),sQuery(id+"F0.wireOp",EDGE,"E18.2.10"),sQuery(id+"F0.wireOp",EDGE,"E18.2.11"),sQuery(id+"F0.wireOp",EDGE,"E18.2.12"),sQuery(id+"F0.wireOp",EDGE,"E18.2.13"),sQuery(id+"F0.wireOp",EDGE,"E18.2.14"),sQuery(id+"F0.wireOp",EDGE,"E18.2.15"),sQuery(id+"F0.wireOp",EDGE,"E19"),sQuery(id+"F0.wireOp",EDGE,"E20"),sQuery(id+"F0.wireOp",EDGE,"E21"),sQuery(id+"F0.wireOp",EDGE,"E22")])],"isStart":true}),makeQuery(id+"F4.opExtrude","SWEPT_FACE",FACE,{"disambiguationData":[OSD([sQuery(id+"F3.wireOp",EDGE,"E34")])]})]}),makeQuery(id+"F7.opPattern","COPY",FACE,{"derivedFrom":makeQuery(id+"F6.opExtrude","CAP_FACE",FACE,{"disambiguationData":[OSD([sQuery(id+"F5.wireOp",EDGE,"E38.2"),sQuery(id+"F5.wireOp",EDGE,"E38.3"),sQuery(id+"F5.wireOp",EDGE,"E38.4"),sQuery(id+"F5.wireOp",EDGE,"E39")])],"isStart":false}),"instanceName":"1"})],"blendedInto":[makeQuery(id+"F7.opPattern","COPY",FACE,{"derivedFrom":makeQuery(id+"F6.opExtrude","CAP_FACE",FACE,{"disambiguationData":[OSD([sQuery(id+"F5.wireOp",EDGE,"E38.2"),sQuery(id+"F5.wireOp",EDGE,"E38.3"),sQuery(id+"F5.wireOp",EDGE,"E38.4"),sQuery(id+"F5.wireOp",EDGE,"E39")])],"isStart":false}),"instanceName":"1"})]});
            var Q14;
            Q14=makeQuery(id+"F8.opFillet","BLEND_EDGE",EDGE,{"blendedFrom":[makeQuery(id+"F4.boolean.opBoolean","INTERSECT",EDGE,{"derivedFrom":[makeQuery(id+"F1.opExtrude","CAP_FACE",FACE,{"disambiguationData":[OSD([sQuery(id+"F0.wireOp",EDGE,"E0"),sQuery(id+"F0.wireOp",EDGE,"E1.2"),sQuery(id+"F0.wireOp",EDGE,"E1.3"),sQuery(id+"F0.wireOp",EDGE,"E1.4"),sQuery(id+"F0.wireOp",EDGE,"E4"),sQuery(id+"F0.wireOp",EDGE,"E5"),sQuery(id+"F0.wireOp",EDGE,"E6.0"),sQuery(id+"F0.wireOp",EDGE,"E6.1"),sQuery(id+"F0.wireOp",EDGE,"E7.filletArc"),sQuery(id+"F0.wireOp",EDGE,"E8.filletArc"),sQuery(id+"F0.wireOp",EDGE,"E10.MirrorCS"),sQuery(id+"F0.wireOp",EDGE,"E11.MirrorCS"),sQuery(id+"F0.wireOp",EDGE,"E12.MirrorCS"),sQuery(id+"F0.wireOp",EDGE,"E13.MirrorCS"),sQuery(id+"F0.wireOp",EDGE,"E14.MirrorCS"),sQuery(id+"F0.wireOp",EDGE,"E15.trimOffspring"),sQuery(id+"F0.wireOp",EDGE,"E16"),sQuery(id+"F0.wireOp",EDGE,"E17"),sQuery(id+"F0.wireOp",EDGE,"E18.1.0"),sQuery(id+"F0.wireOp",EDGE,"E18.1.1"),sQuery(id+"F0.wireOp",EDGE,"E18.1.2"),sQuery(id+"F0.wireOp",EDGE,"E18.1.3"),sQuery(id+"F0.wireOp",EDGE,"E18.1.4"),sQuery(id+"F0.wireOp",EDGE,"E18.1.5"),sQuery(id+"F0.wireOp",EDGE,"E18.1.6"),sQuery(id+"F0.wireOp",EDGE,"E18.1.7"),sQuery(id+"F0.wireOp",EDGE,"E18.1.8"),sQuery(id+"F0.wireOp",EDGE,"E18.1.9"),sQuery(id+"F0.wireOp",EDGE,"E18.1.10"),sQuery(id+"F0.wireOp",EDGE,"E18.1.11"),sQuery(id+"F0.wireOp",EDGE,"E18.1.12"),sQuery(id+"F0.wireOp",EDGE,"E18.1.13"),sQuery(id+"F0.wireOp",EDGE,"E18.1.14"),sQuery(id+"F0.wireOp",EDGE,"E18.1.15"),sQuery(id+"F0.wireOp",EDGE,"E18.2.0"),sQuery(id+"F0.wireOp",EDGE,"E18.2.1"),sQuery(id+"F0.wireOp",EDGE,"E18.2.2"),sQuery(id+"F0.wireOp",EDGE,"E18.2.3"),sQuery(id+"F0.wireOp",EDGE,"E18.2.4"),sQuery(id+"F0.wireOp",EDGE,"E18.2.5"),sQuery(id+"F0.wireOp",EDGE,"E18.2.6"),sQuery(id+"F0.wireOp",EDGE,"E18.2.7"),sQuery(id+"F0.wireOp",EDGE,"E18.2.8"),sQuery(id+"F0.wireOp",EDGE,"E18.2.9"),sQuery(id+"F0.wireOp",EDGE,"E18.2.10"),sQuery(id+"F0.wireOp",EDGE,"E18.2.11"),sQuery(id+"F0.wireOp",EDGE,"E18.2.12"),sQuery(id+"F0.wireOp",EDGE,"E18.2.13"),sQuery(id+"F0.wireOp",EDGE,"E18.2.14"),sQuery(id+"F0.wireOp",EDGE,"E18.2.15"),sQuery(id+"F0.wireOp",EDGE,"E19"),sQuery(id+"F0.wireOp",EDGE,"E20"),sQuery(id+"F0.wireOp",EDGE,"E21"),sQuery(id+"F0.wireOp",EDGE,"E22")])],"isStart":true}),makeQuery(id+"F4.opExtrude","SWEPT_FACE",FACE,{"disambiguationData":[OSD([sQuery(id+"F3.wireOp",EDGE,"E37.1.3")])]})]}),makeQuery(id+"F7.opPattern","COPY",FACE,{"derivedFrom":makeQuery(id+"F6.opExtrude","CAP_FACE",FACE,{"disambiguationData":[OSD([sQuery(id+"F5.wireOp",EDGE,"E42.2.1"),sQuery(id+"F5.wireOp",EDGE,"E42.2.3"),sQuery(id+"F5.wireOp",EDGE,"E42.2.4"),sQuery(id+"F5.wireOp",EDGE,"E42.2.5")])],"isStart":false}),"instanceName":"1"})],"blendedInto":[makeQuery(id+"F7.opPattern","COPY",FACE,{"derivedFrom":makeQuery(id+"F6.opExtrude","CAP_FACE",FACE,{"disambiguationData":[OSD([sQuery(id+"F5.wireOp",EDGE,"E42.2.1"),sQuery(id+"F5.wireOp",EDGE,"E42.2.3"),sQuery(id+"F5.wireOp",EDGE,"E42.2.4"),sQuery(id+"F5.wireOp",EDGE,"E42.2.5")])],"isStart":false}),"instanceName":"1"})]});
            var Q15;
            Q15=makeQuery(id+"F8.opFillet","BLEND_EDGE",EDGE,{"blendedFrom":[makeQuery(id+"F4.boolean.opBoolean","INTERSECT",EDGE,{"derivedFrom":[makeQuery(id+"F1.opExtrude","CAP_FACE",FACE,{"disambiguationData":[OSD([sQuery(id+"F0.wireOp",EDGE,"E0"),sQuery(id+"F0.wireOp",EDGE,"E1.2"),sQuery(id+"F0.wireOp",EDGE,"E1.3"),sQuery(id+"F0.wireOp",EDGE,"E1.4"),sQuery(id+"F0.wireOp",EDGE,"E4"),sQuery(id+"F0.wireOp",EDGE,"E5"),sQuery(id+"F0.wireOp",EDGE,"E6.0"),sQuery(id+"F0.wireOp",EDGE,"E6.1"),sQuery(id+"F0.wireOp",EDGE,"E7.filletArc"),sQuery(id+"F0.wireOp",EDGE,"E8.filletArc"),sQuery(id+"F0.wireOp",EDGE,"E10.MirrorCS"),sQuery(id+"F0.wireOp",EDGE,"E11.MirrorCS"),sQuery(id+"F0.wireOp",EDGE,"E12.MirrorCS"),sQuery(id+"F0.wireOp",EDGE,"E13.MirrorCS"),sQuery(id+"F0.wireOp",EDGE,"E14.MirrorCS"),sQuery(id+"F0.wireOp",EDGE,"E15.trimOffspring"),sQuery(id+"F0.wireOp",EDGE,"E16"),sQuery(id+"F0.wireOp",EDGE,"E17"),sQuery(id+"F0.wireOp",EDGE,"E18.1.0"),sQuery(id+"F0.wireOp",EDGE,"E18.1.1"),sQuery(id+"F0.wireOp",EDGE,"E18.1.2"),sQuery(id+"F0.wireOp",EDGE,"E18.1.3"),sQuery(id+"F0.wireOp",EDGE,"E18.1.4"),sQuery(id+"F0.wireOp",EDGE,"E18.1.5"),sQuery(id+"F0.wireOp",EDGE,"E18.1.6"),sQuery(id+"F0.wireOp",EDGE,"E18.1.7"),sQuery(id+"F0.wireOp",EDGE,"E18.1.8"),sQuery(id+"F0.wireOp",EDGE,"E18.1.9"),sQuery(id+"F0.wireOp",EDGE,"E18.1.10"),sQuery(id+"F0.wireOp",EDGE,"E18.1.11"),sQuery(id+"F0.wireOp",EDGE,"E18.1.12"),sQuery(id+"F0.wireOp",EDGE,"E18.1.13"),sQuery(id+"F0.wireOp",EDGE,"E18.1.14"),sQuery(id+"F0.wireOp",EDGE,"E18.1.15"),sQuery(id+"F0.wireOp",EDGE,"E18.2.0"),sQuery(id+"F0.wireOp",EDGE,"E18.2.1"),sQuery(id+"F0.wireOp",EDGE,"E18.2.2"),sQuery(id+"F0.wireOp",EDGE,"E18.2.3"),sQuery(id+"F0.wireOp",EDGE,"E18.2.4"),sQuery(id+"F0.wireOp",EDGE,"E18.2.5"),sQuery(id+"F0.wireOp",EDGE,"E18.2.6"),sQuery(id+"F0.wireOp",EDGE,"E18.2.7"),sQuery(id+"F0.wireOp",EDGE,"E18.2.8"),sQuery(id+"F0.wireOp",EDGE,"E18.2.9"),sQuery(id+"F0.wireOp",EDGE,"E18.2.10"),sQuery(id+"F0.wireOp",EDGE,"E18.2.11"),sQuery(id+"F0.wireOp",EDGE,"E18.2.12"),sQuery(id+"F0.wireOp",EDGE,"E18.2.13"),sQuery(id+"F0.wireOp",EDGE,"E18.2.14"),sQuery(id+"F0.wireOp",EDGE,"E18.2.15"),sQuery(id+"F0.wireOp",EDGE,"E19"),sQuery(id+"F0.wireOp",EDGE,"E20"),sQuery(id+"F0.wireOp",EDGE,"E21"),sQuery(id+"F0.wireOp",EDGE,"E22")])],"isStart":false}),makeQuery(id+"F4.opExtrude","SWEPT_FACE",FACE,{"disambiguationData":[OSD([sQuery(id+"F3.wireOp",EDGE,"E34")])]})]}),makeQuery(id+"F6.opExtrude","CAP_FACE",FACE,{"disambiguationData":[OSD([sQuery(id+"F5.wireOp",EDGE,"E38.2"),sQuery(id+"F5.wireOp",EDGE,"E38.3"),sQuery(id+"F5.wireOp",EDGE,"E38.4"),sQuery(id+"F5.wireOp",EDGE,"E39")])],"isStart":false})],"blendedInto":[makeQuery(id+"F6.opExtrude","CAP_FACE",FACE,{"disambiguationData":[OSD([sQuery(id+"F5.wireOp",EDGE,"E38.2"),sQuery(id+"F5.wireOp",EDGE,"E38.3"),sQuery(id+"F5.wireOp",EDGE,"E38.4"),sQuery(id+"F5.wireOp",EDGE,"E39")])],"isStart":false})]});
            var Q16;
            Q16=makeQuery(id+"F8.opFillet","BLEND_EDGE",EDGE,{"blendedFrom":[makeQuery(id+"F4.boolean.opBoolean","INTERSECT",EDGE,{"derivedFrom":[makeQuery(id+"F1.opExtrude","CAP_FACE",FACE,{"disambiguationData":[OSD([sQuery(id+"F0.wireOp",EDGE,"E0"),sQuery(id+"F0.wireOp",EDGE,"E1.2"),sQuery(id+"F0.wireOp",EDGE,"E1.3"),sQuery(id+"F0.wireOp",EDGE,"E1.4"),sQuery(id+"F0.wireOp",EDGE,"E4"),sQuery(id+"F0.wireOp",EDGE,"E5"),sQuery(id+"F0.wireOp",EDGE,"E6.0"),sQuery(id+"F0.wireOp",EDGE,"E6.1"),sQuery(id+"F0.wireOp",EDGE,"E7.filletArc"),sQuery(id+"F0.wireOp",EDGE,"E8.filletArc"),sQuery(id+"F0.wireOp",EDGE,"E10.MirrorCS"),sQuery(id+"F0.wireOp",EDGE,"E11.MirrorCS"),sQuery(id+"F0.wireOp",EDGE,"E12.MirrorCS"),sQuery(id+"F0.wireOp",EDGE,"E13.MirrorCS"),sQuery(id+"F0.wireOp",EDGE,"E14.MirrorCS"),sQuery(id+"F0.wireOp",EDGE,"E15.trimOffspring"),sQuery(id+"F0.wireOp",EDGE,"E16"),sQuery(id+"F0.wireOp",EDGE,"E17"),sQuery(id+"F0.wireOp",EDGE,"E18.1.0"),sQuery(id+"F0.wireOp",EDGE,"E18.1.1"),sQuery(id+"F0.wireOp",EDGE,"E18.1.2"),sQuery(id+"F0.wireOp",EDGE,"E18.1.3"),sQuery(id+"F0.wireOp",EDGE,"E18.1.4"),sQuery(id+"F0.wireOp",EDGE,"E18.1.5"),sQuery(id+"F0.wireOp",EDGE,"E18.1.6"),sQuery(id+"F0.wireOp",EDGE,"E18.1.7"),sQuery(id+"F0.wireOp",EDGE,"E18.1.8"),sQuery(id+"F0.wireOp",EDGE,"E18.1.9"),sQuery(id+"F0.wireOp",EDGE,"E18.1.10"),sQuery(id+"F0.wireOp",EDGE,"E18.1.11"),sQuery(id+"F0.wireOp",EDGE,"E18.1.12"),sQuery(id+"F0.wireOp",EDGE,"E18.1.13"),sQuery(id+"F0.wireOp",EDGE,"E18.1.14"),sQuery(id+"F0.wireOp",EDGE,"E18.1.15"),sQuery(id+"F0.wireOp",EDGE,"E18.2.0"),sQuery(id+"F0.wireOp",EDGE,"E18.2.1"),sQuery(id+"F0.wireOp",EDGE,"E18.2.2"),sQuery(id+"F0.wireOp",EDGE,"E18.2.3"),sQuery(id+"F0.wireOp",EDGE,"E18.2.4"),sQuery(id+"F0.wireOp",EDGE,"E18.2.5"),sQuery(id+"F0.wireOp",EDGE,"E18.2.6"),sQuery(id+"F0.wireOp",EDGE,"E18.2.7"),sQuery(id+"F0.wireOp",EDGE,"E18.2.8"),sQuery(id+"F0.wireOp",EDGE,"E18.2.9"),sQuery(id+"F0.wireOp",EDGE,"E18.2.10"),sQuery(id+"F0.wireOp",EDGE,"E18.2.11"),sQuery(id+"F0.wireOp",EDGE,"E18.2.12"),sQuery(id+"F0.wireOp",EDGE,"E18.2.13"),sQuery(id+"F0.wireOp",EDGE,"E18.2.14"),sQuery(id+"F0.wireOp",EDGE,"E18.2.15"),sQuery(id+"F0.wireOp",EDGE,"E19"),sQuery(id+"F0.wireOp",EDGE,"E20"),sQuery(id+"F0.wireOp",EDGE,"E21"),sQuery(id+"F0.wireOp",EDGE,"E22")])],"isStart":false}),makeQuery(id+"F4.opExtrude","SWEPT_FACE",FACE,{"disambiguationData":[OSD([sQuery(id+"F3.wireOp",EDGE,"E37.1.3")])]})]}),makeQuery(id+"F6.opExtrude","CAP_FACE",FACE,{"disambiguationData":[OSD([sQuery(id+"F5.wireOp",EDGE,"E42.2.1"),sQuery(id+"F5.wireOp",EDGE,"E42.2.3"),sQuery(id+"F5.wireOp",EDGE,"E42.2.4"),sQuery(id+"F5.wireOp",EDGE,"E42.2.5")])],"isStart":false})],"blendedInto":[makeQuery(id+"F6.opExtrude","CAP_FACE",FACE,{"disambiguationData":[OSD([sQuery(id+"F5.wireOp",EDGE,"E42.2.1"),sQuery(id+"F5.wireOp",EDGE,"E42.2.3"),sQuery(id+"F5.wireOp",EDGE,"E42.2.4"),sQuery(id+"F5.wireOp",EDGE,"E42.2.5")])],"isStart":false})]});
            var Q17;
            Q17=makeQuery(id+"F8.opFillet","BLEND_EDGE",EDGE,{"blendedFrom":[makeQuery(id+"F4.boolean.opBoolean","INTERSECT",EDGE,{"derivedFrom":[makeQuery(id+"F1.opExtrude","CAP_FACE",FACE,{"disambiguationData":[OSD([sQuery(id+"F0.wireOp",EDGE,"E0"),sQuery(id+"F0.wireOp",EDGE,"E1.2"),sQuery(id+"F0.wireOp",EDGE,"E1.3"),sQuery(id+"F0.wireOp",EDGE,"E1.4"),sQuery(id+"F0.wireOp",EDGE,"E4"),sQuery(id+"F0.wireOp",EDGE,"E5"),sQuery(id+"F0.wireOp",EDGE,"E6.0"),sQuery(id+"F0.wireOp",EDGE,"E6.1"),sQuery(id+"F0.wireOp",EDGE,"E7.filletArc"),sQuery(id+"F0.wireOp",EDGE,"E8.filletArc"),sQuery(id+"F0.wireOp",EDGE,"E10.MirrorCS"),sQuery(id+"F0.wireOp",EDGE,"E11.MirrorCS"),sQuery(id+"F0.wireOp",EDGE,"E12.MirrorCS"),sQuery(id+"F0.wireOp",EDGE,"E13.MirrorCS"),sQuery(id+"F0.wireOp",EDGE,"E14.MirrorCS"),sQuery(id+"F0.wireOp",EDGE,"E15.trimOffspring"),sQuery(id+"F0.wireOp",EDGE,"E16"),sQuery(id+"F0.wireOp",EDGE,"E17"),sQuery(id+"F0.wireOp",EDGE,"E18.1.0"),sQuery(id+"F0.wireOp",EDGE,"E18.1.1"),sQuery(id+"F0.wireOp",EDGE,"E18.1.2"),sQuery(id+"F0.wireOp",EDGE,"E18.1.3"),sQuery(id+"F0.wireOp",EDGE,"E18.1.4"),sQuery(id+"F0.wireOp",EDGE,"E18.1.5"),sQuery(id+"F0.wireOp",EDGE,"E18.1.6"),sQuery(id+"F0.wireOp",EDGE,"E18.1.7"),sQuery(id+"F0.wireOp",EDGE,"E18.1.8"),sQuery(id+"F0.wireOp",EDGE,"E18.1.9"),sQuery(id+"F0.wireOp",EDGE,"E18.1.10"),sQuery(id+"F0.wireOp",EDGE,"E18.1.11"),sQuery(id+"F0.wireOp",EDGE,"E18.1.12"),sQuery(id+"F0.wireOp",EDGE,"E18.1.13"),sQuery(id+"F0.wireOp",EDGE,"E18.1.14"),sQuery(id+"F0.wireOp",EDGE,"E18.1.15"),sQuery(id+"F0.wireOp",EDGE,"E18.2.0"),sQuery(id+"F0.wireOp",EDGE,"E18.2.1"),sQuery(id+"F0.wireOp",EDGE,"E18.2.2"),sQuery(id+"F0.wireOp",EDGE,"E18.2.3"),sQuery(id+"F0.wireOp",EDGE,"E18.2.4"),sQuery(id+"F0.wireOp",EDGE,"E18.2.5"),sQuery(id+"F0.wireOp",EDGE,"E18.2.6"),sQuery(id+"F0.wireOp",EDGE,"E18.2.7"),sQuery(id+"F0.wireOp",EDGE,"E18.2.8"),sQuery(id+"F0.wireOp",EDGE,"E18.2.9"),sQuery(id+"F0.wireOp",EDGE,"E18.2.10"),sQuery(id+"F0.wireOp",EDGE,"E18.2.11"),sQuery(id+"F0.wireOp",EDGE,"E18.2.12"),sQuery(id+"F0.wireOp",EDGE,"E18.2.13"),sQuery(id+"F0.wireOp",EDGE,"E18.2.14"),sQuery(id+"F0.wireOp",EDGE,"E18.2.15"),sQuery(id+"F0.wireOp",EDGE,"E19"),sQuery(id+"F0.wireOp",EDGE,"E20"),sQuery(id+"F0.wireOp",EDGE,"E21"),sQuery(id+"F0.wireOp",EDGE,"E22")])],"isStart":false}),makeQuery(id+"F4.opExtrude","SWEPT_FACE",FACE,{"disambiguationData":[OSD([sQuery(id+"F3.wireOp",EDGE,"E37.2.3")])]})]}),makeQuery(id+"F6.opExtrude","CAP_FACE",FACE,{"disambiguationData":[OSD([sQuery(id+"F5.wireOp",EDGE,"E42.1.1"),sQuery(id+"F5.wireOp",EDGE,"E42.1.3"),sQuery(id+"F5.wireOp",EDGE,"E42.1.4"),sQuery(id+"F5.wireOp",EDGE,"E42.1.5")])],"isStart":false})],"blendedInto":[makeQuery(id+"F6.opExtrude","CAP_FACE",FACE,{"disambiguationData":[OSD([sQuery(id+"F5.wireOp",EDGE,"E42.1.1"),sQuery(id+"F5.wireOp",EDGE,"E42.1.3"),sQuery(id+"F5.wireOp",EDGE,"E42.1.4"),sQuery(id+"F5.wireOp",EDGE,"E42.1.5")])],"isStart":false})]});
            fillet(context, id + "F9", {"entities" : qUnion([Q0, Q1, Q2, Q3, Q4, Q5, Q6, Q7, Q8, Q9, Q10, Q11, Q12, Q13, Q14, Q15, Q16, Q17]), "radius" : 5 * mm, "tangentPropagation" : true, "allowEdgeOverflow" : false});
        }
    });
